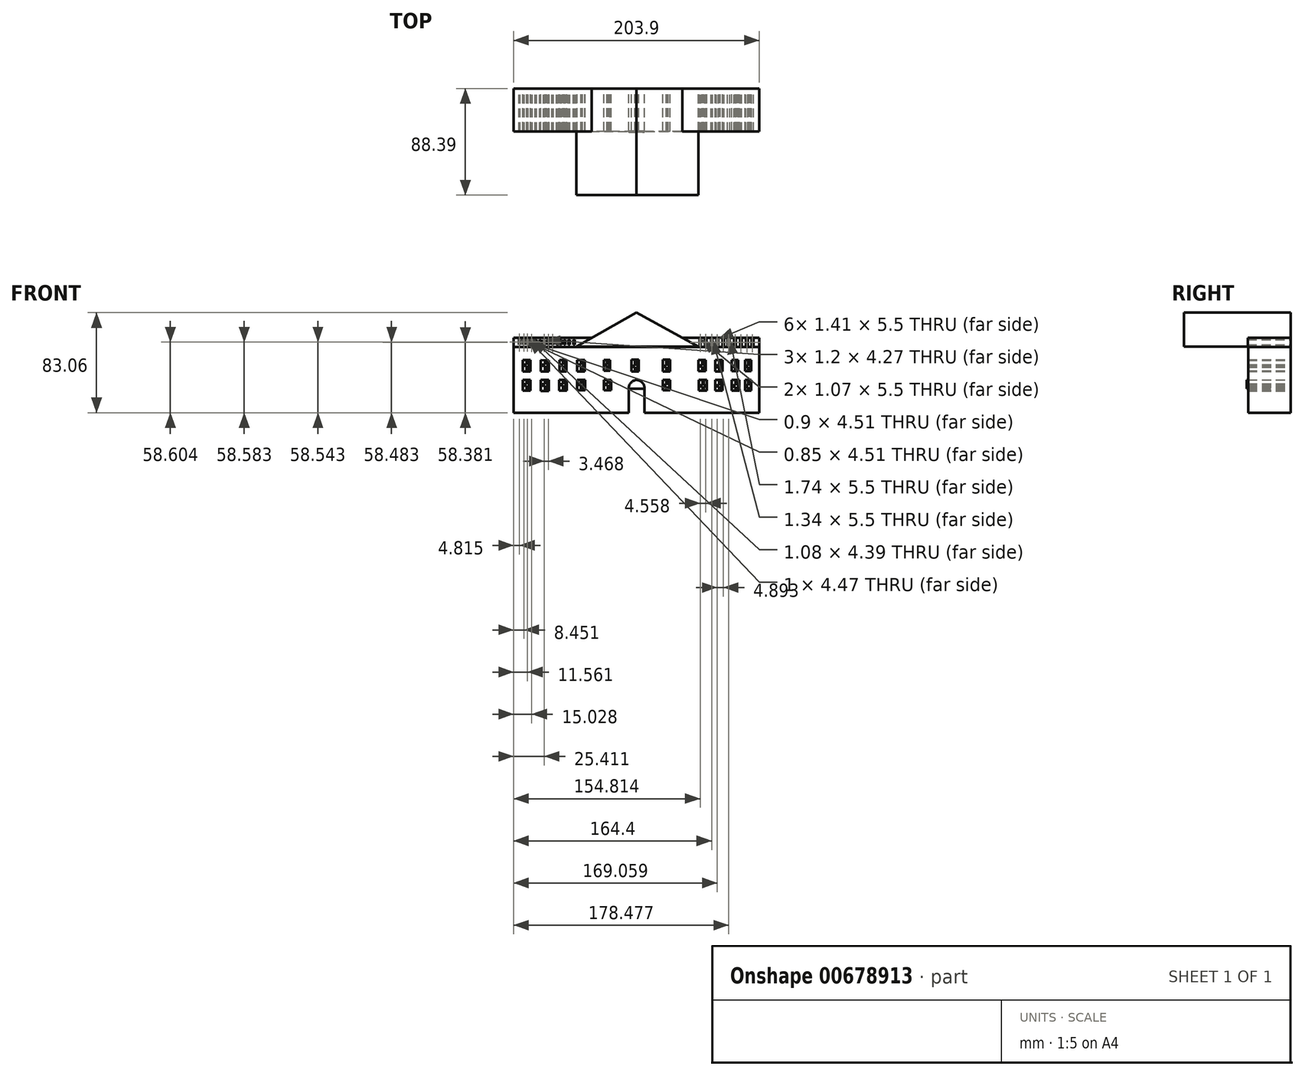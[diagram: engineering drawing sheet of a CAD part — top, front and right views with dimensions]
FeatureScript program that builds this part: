
annotation { "Feature Type Name" : "Feature", "Feature Type Description" : "" }
export const myFeature = defineFeature(function(context is Context, id is Id, definition is map)
    precondition{}
    {
        {
            var Q0;
            Q0=qCreatedBy(makeId("Front.planeOp"),FACE);
            var sketch = newSketch(context, id + "F0", { "sketchPlane" : qUnion([Q0])});
            skLineSegment(sketch, "E0.bottom", {"start": v(-101.95, -27.21) * mm, "end": v(101.95, -27.21) * mm});
            skLineSegment(sketch, "E0.top", {"start": v(-101.95, 27.21) * mm, "end": v(101.95, 27.21) * mm});
            skLineSegment(sketch, "E0.left", {"start": v(-101.95, -27.21) * mm, "end": v(-101.95, 27.21) * mm});
            skLineSegment(sketch, "E0.right", {"start": v(101.95, -27.21) * mm, "end": v(101.95, 27.21) * mm});
            skPoint(sketch, "E0.middle", {"position": v(0, 0) * mm});
            skLineSegment(sketch, "E1", {"start": v(-63.99, 16.59) * mm, "end": v(-63.99, 7.1) * mm});
            skLineSegment(sketch, "E2", {"start": v(-63.99, 16.59) * mm, "end": v(-58.11, 16.59) * mm});
            skLineSegment(sketch, "E3", {"start": v(-58.11, 16.59) * mm, "end": v(-58.11, 7.1) * mm});
            skLineSegment(sketch, "E4", {"start": v(-63.99, 7.1) * mm, "end": v(-58.11, 7.1) * mm});
            skLineSegment(sketch, "E5", {"start": v(-64.18, 0) * mm, "end": v(-64.18, -9) * mm});
            skLineSegment(sketch, "E6", {"start": v(-64.18, 0) * mm, "end": v(-57.73, 0) * mm});
            skLineSegment(sketch, "E7", {"start": v(-57.73, 0) * mm, "end": v(-57.73, -9) * mm});
            skLineSegment(sketch, "E8", {"start": v(-64.18, -9) * mm, "end": v(-57.73, -9) * mm});
            skLineSegment(sketch, "E9", {"start": v(51.48, 16.59) * mm, "end": v(51.48, 7.3) * mm});
            skLineSegment(sketch, "E10", {"start": v(51.48, 16.59) * mm, "end": v(57.54, 16.59) * mm});
            skLineSegment(sketch, "E11", {"start": v(57.54, 16.59) * mm, "end": v(57.54, 7.3) * mm});
            skLineSegment(sketch, "E12", {"start": v(57.54, 7.3) * mm, "end": v(51.48, 7.3) * mm});
            skLineSegment(sketch, "E13", {"start": v(51.67, 0) * mm, "end": v(51.67, -8.82) * mm});
            skLineSegment(sketch, "E14", {"start": v(51.67, -8.82) * mm, "end": v(58.3, -8.82) * mm});
            skLineSegment(sketch, "E15", {"start": v(58.3, -8.82) * mm, "end": v(58.3, 0) * mm});
            skLineSegment(sketch, "E16", {"start": v(58.3, 0) * mm, "end": v(51.67, 0) * mm});
            skLineSegment(sketch, "E17", {"start": v(-63.99, 11.85) * mm, "end": v(-58.11, 11.85) * mm});
            skLineSegment(sketch, "E18", {"start": v(-64.18, -4.5) * mm, "end": v(-57.73, -4.5) * mm});
            skLineSegment(sketch, "E19", {"start": v(51.48, 11.94) * mm, "end": v(57.54, 11.94) * mm});
            skLineSegment(sketch, "E20", {"start": v(54.98, 0) * mm, "end": v(54.98, -8.82) * mm});
            skLineSegment(sketch, "E21", {"start": v(51.67, -4.4) * mm, "end": v(58.3, -4.4) * mm});
            skLineSegment(sketch, "E22", {"start": v(-49.4, 16.59) * mm, "end": v(-49.4, 6.93) * mm});
            skLineSegment(sketch, "E23", {"start": v(-49.4, 16.59) * mm, "end": v(-42.94, 16.59) * mm});
            skLineSegment(sketch, "E24", {"start": v(-42.94, 16.59) * mm, "end": v(-42.94, 6.92) * mm});
            skLineSegment(sketch, "E25", {"start": v(-49.4, 6.93) * mm, "end": v(-42.94, 6.92) * mm});
            skLineSegment(sketch, "E26", {"start": v(-49.4, 11.76) * mm, "end": v(-42.94, 11.75) * mm});
            skLineSegment(sketch, "E27", {"start": v(-49.4, 0) * mm, "end": v(-49.4, -8.46) * mm});
            skLineSegment(sketch, "E28", {"start": v(-49.4, 0) * mm, "end": v(-42.56, 0) * mm});
            skLineSegment(sketch, "E29", {"start": v(-42.56, 0) * mm, "end": v(-42.56, -8.46) * mm});
            skLineSegment(sketch, "E30", {"start": v(-42.56, -8.46) * mm, "end": v(-49.4, -8.46) * mm});
            skLineSegment(sketch, "E31", {"start": v(-49.4, -4.23) * mm, "end": v(-42.56, -4.23) * mm});
            skLineSegment(sketch, "E32", {"start": v(-72.65, 16.38) * mm, "end": v(-72.65, 6.92) * mm});
            skLineSegment(sketch, "E33", {"start": v(-72.65, 6.92) * mm, "end": v(-79.35, 6.92) * mm});
            skLineSegment(sketch, "E34", {"start": v(-79.35, 6.92) * mm, "end": v(-79.35, 16.38) * mm});
            skLineSegment(sketch, "E35", {"start": v(-79.35, 16.38) * mm, "end": v(-72.65, 16.38) * mm});
            skLineSegment(sketch, "E36", {"start": v(-87.88, 6.92) * mm, "end": v(-87.88, 16.59) * mm});
            skLineSegment(sketch, "E37", {"start": v(-87.88, 16.59) * mm, "end": v(-94.32, 16.59) * mm});
            skLineSegment(sketch, "E38", {"start": v(-94.32, 16.59) * mm, "end": v(-94.32, 6.92) * mm});
            skLineSegment(sketch, "E39", {"start": v(-94.32, 6.92) * mm, "end": v(-87.88, 6.92) * mm});
            skLineSegment(sketch, "E40", {"start": v(-72.65, 0) * mm, "end": v(-72.71, -9.2) * mm});
            skLineSegment(sketch, "E41", {"start": v(-72.71, -9.2) * mm, "end": v(-79.35, -9.2) * mm});
            skLineSegment(sketch, "E42", {"start": v(-79.35, -9.2) * mm, "end": v(-79.35, 0) * mm});
            skLineSegment(sketch, "E43", {"start": v(-79.35, 0) * mm, "end": v(-72.65, 0) * mm});
            skLineSegment(sketch, "E44", {"start": v(-94.32, 0) * mm, "end": v(-94.32, -9) * mm});
            skLineSegment(sketch, "E45", {"start": v(-94.32, -9) * mm, "end": v(-87.88, -9) * mm});
            skLineSegment(sketch, "E46", {"start": v(-87.88, -9) * mm, "end": v(-87.88, 0) * mm});
            skLineSegment(sketch, "E47", {"start": v(-87.88, 0) * mm, "end": v(-94.32, 0) * mm});
            skLineSegment(sketch, "E48", {"start": v(65.32, 16.59) * mm, "end": v(65.32, 7.1) * mm});
            skLineSegment(sketch, "E49", {"start": v(65.32, 7.1) * mm, "end": v(71.46, 7.1) * mm});
            skLineSegment(sketch, "E50", {"start": v(71.46, 7.1) * mm, "end": v(71.46, 16.59) * mm});
            skLineSegment(sketch, "E51", {"start": v(65.32, 16.59) * mm, "end": v(71.46, 16.59) * mm});
            skLineSegment(sketch, "E52", {"start": v(65.32, 0) * mm, "end": v(71.46, 0) * mm});
            skLineSegment(sketch, "E53", {"start": v(71.46, 0) * mm, "end": v(71.46, -8.83) * mm});
            skLineSegment(sketch, "E54", {"start": v(71.46, -8.83) * mm, "end": v(65.32, -8.83) * mm});
            skLineSegment(sketch, "E55", {"start": v(65.32, 0) * mm, "end": v(65.32, -8.83) * mm});
            skLineSegment(sketch, "E56", {"start": v(78.97, 16.59) * mm, "end": v(78.97, 7.22) * mm});
            skLineSegment(sketch, "E57", {"start": v(78.97, 7.22) * mm, "end": v(84.47, 7.22) * mm});
            skLineSegment(sketch, "E58", {"start": v(84.47, 7.22) * mm, "end": v(84.47, 16.59) * mm});
            skLineSegment(sketch, "E59", {"start": v(84.47, 16.59) * mm, "end": v(78.97, 16.59) * mm});
            skLineSegment(sketch, "E60", {"start": v(78.97, 0) * mm, "end": v(78.97, -9) * mm});
            skLineSegment(sketch, "E61", {"start": v(78.97, -9) * mm, "end": v(85.22, -9) * mm});
            skLineSegment(sketch, "E62", {"start": v(85.22, -9) * mm, "end": v(85.22, 0) * mm});
            skLineSegment(sketch, "E63", {"start": v(85.22, 0) * mm, "end": v(78.97, 0) * mm});
            skLineSegment(sketch, "E64", {"start": v(-91.1, 16.59) * mm, "end": v(-91.1, 6.92) * mm});
            skLineSegment(sketch, "E65", {"start": v(-94.32, 11.76) * mm, "end": v(-87.88, 11.76) * mm});
            skLineSegment(sketch, "E66", {"start": v(-76, 16.38) * mm, "end": v(-76, 6.92) * mm});
            skPoint(sketch, "E67.endSnap0", {"position": v(-72.65, 11.65) * mm});
            skLineSegment(sketch, "E68", {"start": v(-61.05, 16.59) * mm, "end": v(-61.05, 7.1) * mm});
            skLineSegment(sketch, "E69", {"start": v(-46.17, 16.59) * mm, "end": v(-46.17, 6.93) * mm});
            skLineSegment(sketch, "E70", {"start": v(-91.1, 0) * mm, "end": v(-91.1, -9) * mm});
            skLineSegment(sketch, "E71", {"start": v(-94.32, -4.6) * mm, "end": v(-87.88, -4.6) * mm});
            skLineSegment(sketch, "E72", {"start": v(-76, 0) * mm, "end": v(-76.03, -9.2) * mm});
            skLineSegment(sketch, "E73", {"start": v(-79.35, -4.6) * mm, "end": v(-72.68, -4.6) * mm});
            skLineSegment(sketch, "E74", {"start": v(90.03, 16.59) * mm, "end": v(90.03, 7.45) * mm});
            skLineSegment(sketch, "E75", {"start": v(90.03, 7.45) * mm, "end": v(95.26, 7.45) * mm});
            skLineSegment(sketch, "E76", {"start": v(95.26, 7.45) * mm, "end": v(95.26, 16.59) * mm});
            skLineSegment(sketch, "E77", {"start": v(95.26, 16.59) * mm, "end": v(90.03, 16.59) * mm});
            skLineSegment(sketch, "E78", {"start": v(90.03, 0) * mm, "end": v(90.03, -9) * mm});
            skLineSegment(sketch, "E79", {"start": v(90.03, -9) * mm, "end": v(95.26, -9) * mm});
            skLineSegment(sketch, "E80", {"start": v(95.26, -9) * mm, "end": v(95.26, 0) * mm});
            skLineSegment(sketch, "E81", {"start": v(95.26, 0) * mm, "end": v(90.03, 0) * mm});
            skLineSegment(sketch, "E82", {"start": v(54.5, 16.59) * mm, "end": v(54.5, 7.3) * mm});
            skLineSegment(sketch, "E83", {"start": v(65.32, 11.94) * mm, "end": v(71.46, 11.94) * mm});
            skLineSegment(sketch, "E84", {"start": v(68.39, 16.59) * mm, "end": v(68.39, 7.1) * mm});
            skLineSegment(sketch, "E85", {"start": v(78.97, 11.9) * mm, "end": v(84.47, 11.9) * mm});
            skLineSegment(sketch, "E86", {"start": v(81.72, 16.59) * mm, "end": v(81.72, 7.22) * mm});
            skLineSegment(sketch, "E87", {"start": v(92.64, 16.59) * mm, "end": v(92.64, 7.45) * mm});
            skLineSegment(sketch, "E88", {"start": v(90.03, 11.9) * mm, "end": v(95.26, 11.9) * mm});
            skLineSegment(sketch, "E89", {"start": v(68.39, 0) * mm, "end": v(68.39, -8.83) * mm});
            skLineSegment(sketch, "E90", {"start": v(65.32, -4.42) * mm, "end": v(71.46, -4.42) * mm});
            skLineSegment(sketch, "E91", {"start": v(82.1, 0) * mm, "end": v(82.1, -9) * mm});
            skLineSegment(sketch, "E92", {"start": v(78.97, -4.5) * mm, "end": v(85.22, -4.5) * mm});
            skLineSegment(sketch, "E93", {"start": v(92.64, 0) * mm, "end": v(92.64, -9) * mm});
            skLineSegment(sketch, "E94", {"start": v(90.03, -4.5) * mm, "end": v(95.26, -4.5) * mm});
            skLineSegment(sketch, "E95", {"start": v(-60.96, 0) * mm, "end": v(-60.96, -9) * mm});
            skLineSegment(sketch, "E96", {"start": v(-45.98, 0) * mm, "end": v(-45.98, -8.46) * mm});
            skLineSegment(sketch, "E97.bottom", {"start": v(-27.02, 7.5) * mm, "end": v(-21.9, 7.5) * mm});
            skLineSegment(sketch, "E97.top", {"start": v(-27.02, 16.4) * mm, "end": v(-21.9, 16.4) * mm});
            skLineSegment(sketch, "E97.left", {"start": v(-27.02, 7.5) * mm, "end": v(-27.02, 16.4) * mm});
            skLineSegment(sketch, "E97.right", {"start": v(-21.9, 7.5) * mm, "end": v(-21.9, 16.4) * mm});
            skLineSegment(sketch, "E98.bottom", {"start": v(-4.27, 16.78) * mm, "end": v(1.8, 16.78) * mm});
            skLineSegment(sketch, "E98.top", {"start": v(-4.27, 6.93) * mm, "end": v(1.8, 6.93) * mm});
            skLineSegment(sketch, "E98.left", {"start": v(-4.27, 16.78) * mm, "end": v(-4.27, 6.93) * mm});
            skLineSegment(sketch, "E98.right", {"start": v(1.8, 16.78) * mm, "end": v(1.8, 6.93) * mm});
            skLineSegment(sketch, "E99.bottom", {"start": v(21.7, 16.78) * mm, "end": v(27.78, 16.78) * mm});
            skLineSegment(sketch, "E99.top", {"start": v(21.7, 6.93) * mm, "end": v(27.78, 6.93) * mm});
            skLineSegment(sketch, "E99.left", {"start": v(21.7, 16.78) * mm, "end": v(21.7, 6.93) * mm});
            skLineSegment(sketch, "E99.right", {"start": v(27.78, 16.78) * mm, "end": v(27.78, 6.93) * mm});
            skLineSegment(sketch, "E100.bottom", {"start": v(-27.02, -8.46) * mm, "end": v(-20.95, -8.46) * mm});
            skLineSegment(sketch, "E100.top", {"start": v(-27.02, 0) * mm, "end": v(-20.95, 0) * mm});
            skLineSegment(sketch, "E100.left", {"start": v(-27.02, -8.46) * mm, "end": v(-27.02, 0) * mm});
            skLineSegment(sketch, "E100.right", {"start": v(-20.95, -8.46) * mm, "end": v(-20.95, 0) * mm});
            skLineSegment(sketch, "E101.bottom", {"start": v(21.7, 0) * mm, "end": v(27.78, 0) * mm});
            skLineSegment(sketch, "E101.top", {"start": v(21.7, -8.46) * mm, "end": v(27.78, -8.46) * mm});
            skLineSegment(sketch, "E101.left", {"start": v(21.7, 0) * mm, "end": v(21.7, -8.46) * mm});
            skLineSegment(sketch, "E101.right", {"start": v(27.78, 0) * mm, "end": v(27.78, -8.46) * mm});
            skLineSegment(sketch, "E102.bottom", {"start": v(-6.49, -7.17) * mm, "end": v(6.77, -7.17) * mm});
            skLineSegment(sketch, "E102.top", {"start": v(-6.49, -27.21) * mm, "end": v(6.77, -27.21) * mm});
            skLineSegment(sketch, "E102.left", {"start": v(-6.49, -7.17) * mm, "end": v(-6.49, -27.21) * mm});
            skLineSegment(sketch, "E102.right", {"start": v(6.77, -7.17) * mm, "end": v(6.77, -27.21) * mm});
            skArc(sketch, "E103", {"start": v(-6.49, -7.17) * mm, "mid": v(-4.62, -2.34) * mm, "end": v(0, 0) * mm});
            skArc(sketch, "E104", {"start": v(6.77, -7.17) * mm, "mid": v(4.8, -2.24) * mm, "end": v(0, 0) * mm});
            skLineSegment(sketch, "E105", {"start": v(-4.27, 11.85) * mm, "end": v(1.8, 11.85) * mm});
            skLineSegment(sketch, "E106", {"start": v(-1.23, 16.78) * mm, "end": v(-1.23, 6.93) * mm});
            skLineSegment(sketch, "E107", {"start": v(-24.46, 16.4) * mm, "end": v(-24.46, 7.5) * mm});
            skLineSegment(sketch, "E108", {"start": v(-27.02, 11.95) * mm, "end": v(-21.9, 11.95) * mm});
            skLineSegment(sketch, "E109", {"start": v(-23.98, 0) * mm, "end": v(-23.98, -8.46) * mm});
            skLineSegment(sketch, "E110", {"start": v(-27.02, -4.23) * mm, "end": v(-20.95, -4.23) * mm});
            skLineSegment(sketch, "E111", {"start": v(24.74, 16.78) * mm, "end": v(24.74, 6.93) * mm});
            skLineSegment(sketch, "E112", {"start": v(21.7, 11.85) * mm, "end": v(27.78, 11.85) * mm});
            skLineSegment(sketch, "E113", {"start": v(24.74, 0) * mm, "end": v(24.74, -8.46) * mm});
            skLineSegment(sketch, "E114", {"start": v(21.7, -4.23) * mm, "end": v(27.78, -4.23) * mm});
            skLineSegment(sketch, "E115", {"start": v(-35.12, 27.05) * mm, "end": v(-35.12, -26.82) * mm});
            skLineSegment(sketch, "E116", {"start": v(-37.36, 27.05) * mm, "end": v(-37.36, -26.82) * mm});
            skLineSegment(sketch, "E117", {"start": v(-32.96, -26.82) * mm, "end": v(-32.96, 27.05) * mm});
            skLineSegment(sketch, "E118", {"start": v(-15.86, -26.53) * mm, "end": v(-15.86, 26.88) * mm});
            skLineSegment(sketch, "E119", {"start": v(-10.16, 26.88) * mm, "end": v(-10.16, -26.53) * mm});
            skLineSegment(sketch, "E120", {"start": v(12.5, 26.79) * mm, "end": v(12.5, -26.62) * mm});
            skLineSegment(sketch, "E121", {"start": v(16.1, 26.98) * mm, "end": v(16.1, -26.43) * mm});
            skLineSegment(sketch, "E122", {"start": v(9.23, 26.83) * mm, "end": v(9.23, -26.58) * mm});
            skLineSegment(sketch, "E123", {"start": v(40, 27.01) * mm, "end": v(40, -26.4) * mm});
            skLineSegment(sketch, "E124", {"start": v(33.56, 26.92) * mm, "end": v(33.56, -26.49) * mm});
            skLineSegment(sketch, "E125", {"start": v(-94.32, 12.63) * mm, "end": v(-87.88, 12.63) * mm});
            skLineSegment(sketch, "E126", {"start": v(-72.65, 11.65) * mm, "end": v(-79.35, 11.65) * mm});
            skLineSegment(sketch, "E127", {"start": v(-79.35, 12.63) * mm, "end": v(-72.65, 12.63) * mm});
            skLineSegment(sketch, "E128", {"start": v(-63.99, 12.63) * mm, "end": v(-58.11, 12.63) * mm});
            skLineSegment(sketch, "E129", {"start": v(-49.4, 12.63) * mm, "end": v(-42.94, 12.63) * mm});
            skLineSegment(sketch, "E130", {"start": v(-27.02, 12.63) * mm, "end": v(-21.9, 12.63) * mm});
            skLineSegment(sketch, "E131", {"start": v(-94.32, -3.52) * mm, "end": v(-87.88, -3.52) * mm});
            skLineSegment(sketch, "E132", {"start": v(-79.35, -3.52) * mm, "end": v(-72.67, -3.52) * mm});
            skLineSegment(sketch, "E133", {"start": v(-64.18, -3.52) * mm, "end": v(-57.73, -3.52) * mm});
            skLineSegment(sketch, "E134", {"start": v(-49.4, -3.15) * mm, "end": v(-42.56, -3.15) * mm});
            skLineSegment(sketch, "E135", {"start": v(-27.02, -3.15) * mm, "end": v(-20.95, -3.15) * mm});
            skLineSegment(sketch, "E136", {"start": v(-90.24, 16.59) * mm, "end": v(-90.24, 6.92) * mm});
            skLineSegment(sketch, "E137", {"start": v(-74.78, 16.38) * mm, "end": v(-74.79, 6.92) * mm});
            skLineSegment(sketch, "E138", {"start": v(-90.06, 0) * mm, "end": v(-90.06, -9) * mm});
            skLineSegment(sketch, "E139", {"start": v(-59.94, 16.59) * mm, "end": v(-59.94, 7.1) * mm});
            skLineSegment(sketch, "E140", {"start": v(-74.93, 0) * mm, "end": v(-74.93, -9.2) * mm});
            skLineSegment(sketch, "E141", {"start": v(-59.8, 0) * mm, "end": v(-59.8, -9) * mm});
            skLineSegment(sketch, "E142", {"start": v(-45.1, 16.59) * mm, "end": v(-45.12, 6.92) * mm});
            skLineSegment(sketch, "E143", {"start": v(-44.74, 0) * mm, "end": v(-44.74, -8.46) * mm});
            skLineSegment(sketch, "E144", {"start": v(-23.61, 16.4) * mm, "end": v(-23.61, 7.5) * mm});
            skLineSegment(sketch, "E145", {"start": v(-22.73, 0) * mm, "end": v(-22.73, -8.46) * mm});
            skLineSegment(sketch, "E146", {"start": v(-4.27, 10.73) * mm, "end": v(1.8, 10.73) * mm});
            skLineSegment(sketch, "E147", {"start": v(0, 16.78) * mm, "end": v(0, 6.93) * mm});
            skLineSegment(sketch, "E148", {"start": v(26.02, 16.78) * mm, "end": v(26.02, 6.93) * mm});
            skLineSegment(sketch, "E149", {"start": v(21.7, 10.73) * mm, "end": v(27.78, 10.73) * mm});
            skLineSegment(sketch, "E150", {"start": v(26.24, 0) * mm, "end": v(26.24, -8.46) * mm});
            skLineSegment(sketch, "E151", {"start": v(21.7, -5.43) * mm, "end": v(27.78, -5.43) * mm});
            skLineSegment(sketch, "E152", {"start": v(55.41, 16.59) * mm, "end": v(55.41, 7.3) * mm});
            skLineSegment(sketch, "E153", {"start": v(51.48, 11.02) * mm, "end": v(57.54, 11.02) * mm});
            skLineSegment(sketch, "E154", {"start": v(56, 0) * mm, "end": v(56, -8.82) * mm});
            skLineSegment(sketch, "E155", {"start": v(51.67, -5.43) * mm, "end": v(58.3, -5.43) * mm});
            skLineSegment(sketch, "E156", {"start": v(69.45, 0) * mm, "end": v(69.45, -8.83) * mm});
            skLineSegment(sketch, "E157", {"start": v(65.32, -5.5) * mm, "end": v(71.46, -5.5) * mm});
            skLineSegment(sketch, "E158", {"start": v(69.52, 16.59) * mm, "end": v(69.52, 7.1) * mm});
            skLineSegment(sketch, "E159", {"start": v(65.32, 10.65) * mm, "end": v(71.46, 10.65) * mm});
            skLineSegment(sketch, "E160", {"start": v(82.75, 16.59) * mm, "end": v(82.75, 7.22) * mm});
            skLineSegment(sketch, "E161", {"start": v(78.97, 10.8) * mm, "end": v(84.47, 10.8) * mm});
            skLineSegment(sketch, "E162", {"start": v(83.4, 0) * mm, "end": v(83.4, -9) * mm});
            skLineSegment(sketch, "E163", {"start": v(78.97, -5.72) * mm, "end": v(85.22, -5.72) * mm});
            skLineSegment(sketch, "E164", {"start": v(93.93, 0) * mm, "end": v(93.93, -9) * mm});
            skLineSegment(sketch, "E165", {"start": v(90.03, -5.94) * mm, "end": v(95.26, -5.94) * mm});
            skLineSegment(sketch, "E166", {"start": v(93.5, 16.59) * mm, "end": v(93.6, 7.45) * mm});
            skLineSegment(sketch, "E167", {"start": v(90.03, 10.8) * mm, "end": v(95.26, 10.8) * mm});
            skLineSegment(sketch, "E168", {"start": v(36.76, -26.49) * mm, "end": v(36.76, 26.92) * mm});
            skLineSegment(sketch, "E169", {"start": v(0, 55.85) * mm, "end": v(-49.85, 27.58) * mm});
            skLineSegment(sketch, "E170", {"start": v(0, 55.85) * mm, "end": v(51.4, 27.5) * mm});
            skLineSegment(sketch, "E171", {"start": v(-49.85, 27.58) * mm, "end": v(51.4, 27.5) * mm});
            skLineSegment(sketch, "E172", {"start": v(-13.08, 26.64) * mm, "end": v(-13.08, -26.53) * mm});
            skLineSegment(sketch, "E173", {"start": v(-101.95, 27.21) * mm, "end": v(-101.95, 34.84) * mm});
            skLineSegment(sketch, "E174", {"start": v(-101.95, 34.84) * mm, "end": v(-37.05, 34.84) * mm});
            skLineSegment(sketch, "E175", {"start": v(101.95, 27.21) * mm, "end": v(101.95, 34.84) * mm});
            skLineSegment(sketch, "E176", {"start": v(38.1, 34.84) * mm, "end": v(101.95, 34.84) * mm});
            skLineSegment(sketch, "E177", {"start": v(-97.59, 33.65) * mm, "end": v(-97.59, 29.14) * mm});
            skLineSegment(sketch, "E178", {"start": v(-97.59, 29.14) * mm, "end": v(-96.68, 29.14) * mm});
            skLineSegment(sketch, "E179", {"start": v(-96.68, 29.14) * mm, "end": v(-96.68, 33.65) * mm});
            skLineSegment(sketch, "E180", {"start": v(-96.68, 33.65) * mm, "end": v(-97.59, 33.65) * mm});
            skLineSegment(sketch, "E181", {"start": v(-93.92, 33.65) * mm, "end": v(-93.92, 29.14) * mm});
            skLineSegment(sketch, "E182", {"start": v(-93.92, 33.65) * mm, "end": v(-93.08, 33.65) * mm});
            skLineSegment(sketch, "E183", {"start": v(-93.08, 33.65) * mm, "end": v(-93.08, 29.14) * mm});
            skLineSegment(sketch, "E184", {"start": v(-93.92, 29.14) * mm, "end": v(-93.08, 29.14) * mm});
            skLineSegment(sketch, "E185.bottom", {"start": v(-90.89, 29.14) * mm, "end": v(-89.9, 29.14) * mm});
            skLineSegment(sketch, "E185.top", {"start": v(-90.89, 33.6) * mm, "end": v(-89.9, 33.6) * mm});
            skLineSegment(sketch, "E185.left", {"start": v(-90.89, 29.14) * mm, "end": v(-90.89, 33.6) * mm});
            skLineSegment(sketch, "E185.right", {"start": v(-89.9, 29.14) * mm, "end": v(-89.9, 33.6) * mm});
            skLineSegment(sketch, "E186.bottom", {"start": v(-87.46, 29.14) * mm, "end": v(-86.38, 29.14) * mm});
            skLineSegment(sketch, "E186.top", {"start": v(-87.46, 33.53) * mm, "end": v(-86.38, 33.53) * mm});
            skLineSegment(sketch, "E186.left", {"start": v(-87.46, 29.14) * mm, "end": v(-87.46, 33.53) * mm});
            skLineSegment(sketch, "E186.right", {"start": v(-86.38, 29.14) * mm, "end": v(-86.38, 33.53) * mm});
            skLineSegment(sketch, "E187.bottom", {"start": v(-84.03, 29.14) * mm, "end": v(-82.8, 29.14) * mm});
            skLineSegment(sketch, "E187.top", {"start": v(-84.03, 33.45) * mm, "end": v(-82.8, 33.45) * mm});
            skLineSegment(sketch, "E187.left", {"start": v(-84.03, 29.14) * mm, "end": v(-84.03, 33.45) * mm});
            skLineSegment(sketch, "E187.right", {"start": v(-82.8, 29.14) * mm, "end": v(-82.8, 33.45) * mm});
            skLineSegment(sketch, "E188.bottom", {"start": v(-80.29, 29.14) * mm, "end": v(-79.33, 29.14) * mm});
            skLineSegment(sketch, "E188.top", {"start": v(-80.29, 33.4) * mm, "end": v(-79.33, 33.4) * mm});
            skLineSegment(sketch, "E188.left", {"start": v(-80.29, 29.14) * mm, "end": v(-80.29, 33.4) * mm});
            skLineSegment(sketch, "E188.right", {"start": v(-79.33, 29.14) * mm, "end": v(-79.33, 33.4) * mm});
            skLineSegment(sketch, "E189.bottom", {"start": v(-77.14, 29.14) * mm, "end": v(-75.94, 29.14) * mm});
            skLineSegment(sketch, "E189.top", {"start": v(-77.14, 33.4) * mm, "end": v(-75.94, 33.4) * mm});
            skLineSegment(sketch, "E189.left", {"start": v(-77.14, 29.14) * mm, "end": v(-77.14, 33.4) * mm});
            skLineSegment(sketch, "E189.right", {"start": v(-75.94, 29.14) * mm, "end": v(-75.94, 33.4) * mm});
            skLineSegment(sketch, "E190.bottom", {"start": v(-73.67, 29.14) * mm, "end": v(-72.47, 29.14) * mm});
            skLineSegment(sketch, "E190.top", {"start": v(-73.67, 33.4) * mm, "end": v(-72.47, 33.4) * mm});
            skLineSegment(sketch, "E190.left", {"start": v(-73.67, 29.14) * mm, "end": v(-73.67, 33.4) * mm});
            skLineSegment(sketch, "E190.right", {"start": v(-72.47, 29.14) * mm, "end": v(-72.47, 33.4) * mm});
            skLineSegment(sketch, "E191.bottom", {"start": v(-70.12, 29.14) * mm, "end": v(-68.93, 29.14) * mm});
            skLineSegment(sketch, "E191.top", {"start": v(-70.12, 33.4) * mm, "end": v(-68.93, 33.4) * mm});
            skLineSegment(sketch, "E191.left", {"start": v(-70.12, 29.14) * mm, "end": v(-70.12, 33.4) * mm});
            skLineSegment(sketch, "E191.right", {"start": v(-68.93, 29.14) * mm, "end": v(-68.93, 33.4) * mm});
            skLineSegment(sketch, "E192.bottom", {"start": v(-66.29, 29.14) * mm, "end": v(-65.25, 29.14) * mm});
            skLineSegment(sketch, "E192.top", {"start": v(-66.29, 33.4) * mm, "end": v(-65.25, 33.4) * mm});
            skLineSegment(sketch, "E192.left", {"start": v(-66.29, 29.14) * mm, "end": v(-66.29, 33.4) * mm});
            skLineSegment(sketch, "E192.right", {"start": v(-65.25, 29.14) * mm, "end": v(-65.25, 33.4) * mm});
            skLineSegment(sketch, "E193.bottom", {"start": v(-63.17, 29.14) * mm, "end": v(-62.2, 29.14) * mm});
            skLineSegment(sketch, "E193.top", {"start": v(-63.17, 33.4) * mm, "end": v(-62.2, 33.4) * mm});
            skLineSegment(sketch, "E193.left", {"start": v(-63.17, 29.14) * mm, "end": v(-63.17, 33.4) * mm});
            skLineSegment(sketch, "E193.right", {"start": v(-62.2, 29.14) * mm, "end": v(-62.2, 33.4) * mm});
            skLineSegment(sketch, "E194.bottom", {"start": v(-60.14, 29.14) * mm, "end": v(-58.97, 29.14) * mm});
            skLineSegment(sketch, "E194.top", {"start": v(-60.14, 33.4) * mm, "end": v(-58.97, 33.4) * mm});
            skLineSegment(sketch, "E194.left", {"start": v(-60.14, 29.14) * mm, "end": v(-60.14, 33.4) * mm});
            skLineSegment(sketch, "E194.right", {"start": v(-58.97, 29.14) * mm, "end": v(-58.97, 33.4) * mm});
            skLineSegment(sketch, "E195.bottom", {"start": v(-56.6, 29.14) * mm, "end": v(-55.37, 29.14) * mm});
            skLineSegment(sketch, "E195.top", {"start": v(-56.6, 33.4) * mm, "end": v(-55.37, 33.4) * mm});
            skLineSegment(sketch, "E195.left", {"start": v(-56.6, 29.14) * mm, "end": v(-56.6, 33.4) * mm});
            skLineSegment(sketch, "E195.right", {"start": v(-55.37, 29.14) * mm, "end": v(-55.37, 33.4) * mm});
            skLineSegment(sketch, "E196.bottom", {"start": v(-52.31, 29.1) * mm, "end": v(-51.3, 29.1) * mm});
            skLineSegment(sketch, "E196.top", {"start": v(-52.31, 33.45) * mm, "end": v(-51.3, 33.45) * mm});
            skLineSegment(sketch, "E196.left", {"start": v(-52.31, 29.1) * mm, "end": v(-52.31, 33.45) * mm});
            skLineSegment(sketch, "E196.right", {"start": v(-51.3, 29.1) * mm, "end": v(-51.3, 33.45) * mm});
            skLineSegment(sketch, "E197.bottom", {"start": v(52.33, 28.42) * mm, "end": v(53.4, 28.42) * mm});
            skLineSegment(sketch, "E197.top", {"start": v(52.33, 33.92) * mm, "end": v(53.4, 33.92) * mm});
            skLineSegment(sketch, "E197.left", {"start": v(52.33, 28.42) * mm, "end": v(52.33, 33.92) * mm});
            skLineSegment(sketch, "E197.right", {"start": v(53.4, 28.42) * mm, "end": v(53.4, 33.92) * mm});
            skLineSegment(sketch, "E198.bottom", {"start": v(56.89, 28.42) * mm, "end": v(57.96, 28.42) * mm});
            skLineSegment(sketch, "E198.top", {"start": v(56.89, 33.92) * mm, "end": v(57.96, 33.92) * mm});
            skLineSegment(sketch, "E198.left", {"start": v(56.89, 28.42) * mm, "end": v(56.89, 33.92) * mm});
            skLineSegment(sketch, "E198.right", {"start": v(57.96, 28.42) * mm, "end": v(57.96, 33.92) * mm});
            skLineSegment(sketch, "E199.bottom", {"start": v(61.78, 28.42) * mm, "end": v(63.12, 28.42) * mm});
            skLineSegment(sketch, "E199.top", {"start": v(61.78, 33.92) * mm, "end": v(63.12, 33.92) * mm});
            skLineSegment(sketch, "E199.left", {"start": v(61.78, 28.42) * mm, "end": v(61.78, 33.92) * mm});
            skLineSegment(sketch, "E199.right", {"start": v(63.12, 28.42) * mm, "end": v(63.12, 33.92) * mm});
            skLineSegment(sketch, "E200.bottom", {"start": v(66.4, 28.42) * mm, "end": v(67.81, 28.42) * mm});
            skLineSegment(sketch, "E200.top", {"start": v(66.4, 33.92) * mm, "end": v(67.81, 33.92) * mm});
            skLineSegment(sketch, "E200.left", {"start": v(66.4, 28.42) * mm, "end": v(66.4, 33.92) * mm});
            skLineSegment(sketch, "E200.right", {"start": v(67.81, 28.42) * mm, "end": v(67.81, 33.92) * mm});
            skLineSegment(sketch, "E201.bottom", {"start": v(71.3, 28.42) * mm, "end": v(72.7, 28.42) * mm});
            skLineSegment(sketch, "E201.top", {"start": v(71.3, 33.92) * mm, "end": v(72.7, 33.92) * mm});
            skLineSegment(sketch, "E201.left", {"start": v(71.3, 28.42) * mm, "end": v(71.3, 33.92) * mm});
            skLineSegment(sketch, "E201.right", {"start": v(72.7, 28.42) * mm, "end": v(72.7, 33.92) * mm});
            skLineSegment(sketch, "E202.bottom", {"start": v(75.66, 28.42) * mm, "end": v(77.4, 28.42) * mm});
            skLineSegment(sketch, "E202.top", {"start": v(75.66, 33.92) * mm, "end": v(77.4, 33.92) * mm});
            skLineSegment(sketch, "E202.left", {"start": v(75.66, 28.42) * mm, "end": v(75.66, 33.92) * mm});
            skLineSegment(sketch, "E202.right", {"start": v(77.4, 28.42) * mm, "end": v(77.4, 33.92) * mm});
            skLineSegment(sketch, "E203.bottom", {"start": v(81.02, 28.42) * mm, "end": v(82.43, 28.42) * mm});
            skLineSegment(sketch, "E203.top", {"start": v(81.02, 33.92) * mm, "end": v(82.43, 33.92) * mm});
            skLineSegment(sketch, "E203.left", {"start": v(81.02, 28.42) * mm, "end": v(81.02, 33.92) * mm});
            skLineSegment(sketch, "E203.right", {"start": v(82.43, 28.42) * mm, "end": v(82.43, 33.92) * mm});
            skLineSegment(sketch, "E204.bottom", {"start": v(85.84, 28.42) * mm, "end": v(87.25, 28.42) * mm});
            skLineSegment(sketch, "E204.top", {"start": v(85.84, 33.92) * mm, "end": v(87.25, 33.92) * mm});
            skLineSegment(sketch, "E204.left", {"start": v(85.84, 28.42) * mm, "end": v(85.84, 33.92) * mm});
            skLineSegment(sketch, "E204.right", {"start": v(87.25, 28.42) * mm, "end": v(87.25, 33.92) * mm});
            skLineSegment(sketch, "E205.bottom", {"start": v(90.87, 28.42) * mm, "end": v(92.28, 28.42) * mm});
            skLineSegment(sketch, "E205.top", {"start": v(90.87, 33.92) * mm, "end": v(92.28, 33.92) * mm});
            skLineSegment(sketch, "E205.left", {"start": v(90.87, 28.42) * mm, "end": v(90.87, 33.92) * mm});
            skLineSegment(sketch, "E205.right", {"start": v(92.28, 28.42) * mm, "end": v(92.28, 33.92) * mm});
            skLineSegment(sketch, "E206.bottom", {"start": v(95.56, 28.42) * mm, "end": v(96.97, 28.42) * mm});
            skLineSegment(sketch, "E206.top", {"start": v(95.56, 33.92) * mm, "end": v(96.97, 33.92) * mm});
            skLineSegment(sketch, "E206.left", {"start": v(95.56, 28.42) * mm, "end": v(95.56, 33.92) * mm});
            skLineSegment(sketch, "E206.right", {"start": v(96.97, 28.42) * mm, "end": v(96.97, 33.92) * mm});
            skPoint(sketch, "E207.middle", {"position": v(0, -11.28) * mm});
            skLineSegment(sketch, "E208.top", {"start": v(0, -27.21) * mm, "end": v(-4.96, -27.21) * mm});
            skLineSegment(sketch, "E209.top", {"start": v(0, -27.21) * mm, "end": v(5.04, -27.21) * mm});
            skSolve(sketch);
        }
        {
            var Q0;
            Q0=sQuery(id+"F0.wireOp",EDGE,"E119");
            var Q1;
            Q1=sQuery(id+"F0.wireOp",EDGE,"E118");
            var Q2;
            Q2=sQuery(id+"F0.wireOp",EDGE,"E172");
            revolve(context, id + "F1", {"bodyType" : ToolBodyType.SURFACE, "surfaceOperationType" : NewSurfaceOperationType.NEW, "surfaceEntities" : qUnion([Q0, Q1]), "axis" : qUnion([Q2]), "revolveType" : RevolveType.FULL});
        }
        {
            var Q0;
            Q0=sQuery(id+"F0.wireOp",EDGE,"E121");
            var Q1;
            Q1=sQuery(id+"F0.wireOp",EDGE,"E122");
            var Q2;
            Q2=sQuery(id+"F0.wireOp",EDGE,"E120");
            revolve(context, id + "F2", {"bodyType" : ToolBodyType.SURFACE, "surfaceOperationType" : NewSurfaceOperationType.NEW, "surfaceEntities" : qUnion([Q0, Q1]), "axis" : qUnion([Q2]), "revolveType" : RevolveType.FULL});
        }
        {
            var Q0;
            Q0=sQuery(id+"F0.wireOp",EDGE,"E117");
            var Q1;
            Q1=sQuery(id+"F0.wireOp",EDGE,"E116");
            var Q2;
            Q2=sQuery(id+"F0.wireOp",EDGE,"E115");
            revolve(context, id + "F3", {"bodyType" : ToolBodyType.SURFACE, "surfaceOperationType" : NewSurfaceOperationType.NEW, "surfaceEntities" : qUnion([Q0, Q1]), "axis" : qUnion([Q2]), "revolveType" : RevolveType.FULL});
        }
        {
            var Q0;
            Q0=sQuery(id+"F0.wireOp",EDGE,"E123");
            var Q1;
            Q1=sQuery(id+"F0.wireOp",EDGE,"E124");
            var Q2;
            Q2=sQuery(id+"F0.wireOp",EDGE,"E168");
            revolve(context, id + "F4", {"bodyType" : ToolBodyType.SURFACE, "surfaceOperationType" : NewSurfaceOperationType.NEW, "surfaceEntities" : qUnion([Q0, Q1]), "axis" : qUnion([Q2]), "revolveType" : RevolveType.FULL});
        }
        {
            var Q0;
            Q0=makeQuery(id+"F2.opRevolve","SWEPT_BODY",BODY,{"disambiguationData":[OSD([sQuery(id+"F0.wireOp",EDGE,"E121")])]});
            var Q1;
            Q1=makeQuery(id+"F1.opRevolve","SWEPT_BODY",BODY,{"disambiguationData":[OSD([sQuery(id+"F0.wireOp",EDGE,"E119")])]});
            var Q2;
            Q2=makeQuery(id+"F4.opRevolve","SWEPT_BODY",BODY,{"disambiguationData":[OSD([sQuery(id+"F0.wireOp",EDGE,"E123")])]});
            var Q3;
            Q3=makeQuery(id+"F3.opRevolve","SWEPT_BODY",BODY,{"disambiguationData":[OSD([sQuery(id+"F0.wireOp",EDGE,"E116")])]});
            transform(context, id + "F5", {"entities" : qUnion([Q0, Q1, Q2, Q3]), "transformType" : TransformType.TRANSLATION_3D, "dx" : 0.25 * mm, "dy" : -82.3 * mm, "dz" : 0.5 * mm, "makeCopy" : true});
        }
        {
            var Q0;
            Q0=makeQuery(id+"F3.opRevolve","SWEPT_BODY",BODY,{"disambiguationData":[OSD([sQuery(id+"F0.wireOp",EDGE,"E116")])]});
            var Q1;
            Q1=makeQuery(id+"F1.opRevolve","SWEPT_BODY",BODY,{"disambiguationData":[OSD([sQuery(id+"F0.wireOp",EDGE,"E119")])]});
            var Q2;
            Q2=makeQuery(id+"F4.opRevolve","SWEPT_BODY",BODY,{"disambiguationData":[OSD([sQuery(id+"F0.wireOp",EDGE,"E123")])]});
            var Q3;
            Q3=makeQuery(id+"F2.opRevolve","SWEPT_BODY",BODY,{"disambiguationData":[OSD([sQuery(id+"F0.wireOp",EDGE,"E121")])]});
            transform(context, id + "F6", {"entities" : qUnion([Q0, Q1, Q2, Q3]), "transformType" : TransformType.TRANSLATION_3D, "dx" : 0 * mm, "dy" : -57.15 * mm, "dz" : 0.76 * mm, "makeCopy" : false});
        }
        {
            var Q0;
            Q0=makeQuery(id+"F3.opRevolve","SWEPT_BODY",BODY,{"disambiguationData":[OSD([sQuery(id+"F0.wireOp",EDGE,"E117")])]});
            var Q1;
            Q1=makeQuery(id+"F1.opRevolve","SWEPT_BODY",BODY,{"disambiguationData":[OSD([sQuery(id+"F0.wireOp",EDGE,"E118")])]});
            var Q2;
            Q2=makeQuery(id+"F2.opRevolve","SWEPT_BODY",BODY,{"disambiguationData":[OSD([sQuery(id+"F0.wireOp",EDGE,"E122")])]});
            var Q3;
            Q3=makeQuery(id+"F4.opRevolve","SWEPT_BODY",BODY,{"disambiguationData":[OSD([sQuery(id+"F0.wireOp",EDGE,"E124")])]});
            transform(context, id + "F7", {"entities" : qUnion([Q0, Q1, Q2, Q3]), "transformType" : TransformType.TRANSLATION_3D, "dx" : 0 * mm, "dy" : -44.96 * mm, "dz" : 1.27 * mm, "makeCopy" : false});
        }
        {
            var Q0;
            {var subQ250=sQuery(id+"F0.wireOp",EDGE,"E0.left");Q0=makeQuery(id+"F0.imprint","IMPRINT",FACE,{"disambiguationData":[TD([[makeQuery(id+"F0.imprint","IMPRINT",EDGE,{"derivedFrom":subQ250}),-1.0]])]});}
            extrude(context, id + "F8", {"entities" : qUnion([Q0]), "depth" : 35.3 * mm, "offsetDistance" : 25.4 * mm});
        }
        {
            var Q0;
            Q0=makeQuery(id+"F0.imprint","IMPRINT",FACE,{"disambiguationData":[TD([[makeQuery(id+"F0.imprint","IMPRINT",EDGE,{"derivedFrom":sQuery(id+"F0.wireOp",EDGE,"E169")}),1.0]])]});
            extrude(context, id + "F9", {"entities" : qUnion([Q0]), "depth" : 88.4 * mm, "offsetDistance" : 25.4 * mm});
        }
        {
            var Q0;
            {var subQ0=sQuery(id+"F0.wireOp",EDGE,"E171");Q0=makeQuery(id+"F0.imprint","IMPRINT",FACE,{"disambiguationData":[TD([[makeQuery(id+"F0.imprint","IMPRINT",EDGE,{"derivedFrom":subQ0}),-1.0]])]});}
            extrude(context, id + "F10", {"entities" : qUnion([Q0]), "depth" : 35.56 * mm, "offsetDistance" : 25.4 * mm});
        }
        {
            var Q0;
            {var subQ0=sQuery(id+"F0.wireOp",EDGE,"E64");var subQ1=sQuery(id+"F0.wireOp",EDGE,"E37");var subQ2=makeQuery(id+"F0.imprint","INTERSECT",VERTEX,{"derivedFrom":[subQ1,subQ0]});Q0=makeQuery(id+"F0.imprint","IMPRINT",FACE,{"disambiguationData":[TD([[makeQuery(id+"F0.imprint","IMPRINT",EDGE,{"disambiguationData":[TD([[subQ2,1.0]])],"derivedFrom":subQ1}),1.0]])]});}
            var Q1;
            {var subQ0=sQuery(id+"F0.wireOp",EDGE,"E64");var subQ1=sQuery(id+"F0.wireOp",EDGE,"E39");var subQ2=makeQuery(id+"F0.imprint","INTERSECT",VERTEX,{"derivedFrom":[subQ1,subQ0]});Q1=makeQuery(id+"F0.imprint","IMPRINT",FACE,{"disambiguationData":[TD([[makeQuery(id+"F0.imprint","IMPRINT",EDGE,{"disambiguationData":[TD([[subQ2,-1.0]])],"derivedFrom":subQ1}),1.0]])]});}
            var Q2;
            {var subQ0=sQuery(id+"F0.wireOp",EDGE,"E65");var subQ1=sQuery(id+"F0.wireOp",EDGE,"E36");var subQ2=makeQuery(id+"F0.imprint","INTERSECT",VERTEX,{"derivedFrom":[subQ1,subQ0]});Q2=makeQuery(id+"F0.imprint","IMPRINT",FACE,{"disambiguationData":[TD([[makeQuery(id+"F0.imprint","IMPRINT",EDGE,{"disambiguationData":[TD([[subQ2,-1.0]])],"derivedFrom":subQ1}),1.0]])]});}
            var Q3;
            {var subQ0=sQuery(id+"F0.wireOp",EDGE,"E65");var subQ1=sQuery(id+"F0.wireOp",EDGE,"E38");var subQ2=makeQuery(id+"F0.imprint","INTERSECT",VERTEX,{"derivedFrom":[subQ1,subQ0]});Q3=makeQuery(id+"F0.imprint","IMPRINT",FACE,{"disambiguationData":[TD([[makeQuery(id+"F0.imprint","IMPRINT",EDGE,{"disambiguationData":[TD([[subQ2,1.0]])],"derivedFrom":subQ1}),1.0]])]});}
            var Q4;
            {var subQ0=sQuery(id+"F0.wireOp",EDGE,"E66");var subQ1=sQuery(id+"F0.wireOp",EDGE,"E35");var subQ2=makeQuery(id+"F0.imprint","INTERSECT",VERTEX,{"derivedFrom":[subQ1,subQ0]});Q4=makeQuery(id+"F0.imprint","IMPRINT",FACE,{"disambiguationData":[TD([[makeQuery(id+"F0.imprint","IMPRINT",EDGE,{"disambiguationData":[TD([[subQ2,-1.0]])],"derivedFrom":subQ1}),-1.0]])]});}
            var Q5;
            {var subQ0=sQuery(id+"F0.wireOp",EDGE,"E126");var subQ1=sQuery(id+"F0.wireOp",EDGE,"E34");var subQ2=makeQuery(id+"F0.imprint","INTERSECT",VERTEX,{"derivedFrom":[subQ1,subQ0]});Q5=makeQuery(id+"F0.imprint","IMPRINT",FACE,{"disambiguationData":[TD([[makeQuery(id+"F0.imprint","IMPRINT",EDGE,{"disambiguationData":[TD([[subQ2,-1.0]])],"derivedFrom":subQ1}),-1.0]])]});}
            var Q6;
            {var subQ0=sQuery(id+"F0.wireOp",EDGE,"E126");var subQ1=sQuery(id+"F0.wireOp",EDGE,"E32");var subQ2=makeQuery(id+"F0.imprint","INTERSECT",VERTEX,{"derivedFrom":[subQ1,subQ0]});Q6=makeQuery(id+"F0.imprint","IMPRINT",FACE,{"disambiguationData":[TD([[makeQuery(id+"F0.imprint","IMPRINT",EDGE,{"disambiguationData":[TD([[subQ2,1.0]])],"derivedFrom":subQ1}),-1.0]])]});}
            var Q7;
            {var subQ0=sQuery(id+"F0.wireOp",EDGE,"E66");var subQ1=sQuery(id+"F0.wireOp",EDGE,"E33");var subQ2=makeQuery(id+"F0.imprint","INTERSECT",VERTEX,{"derivedFrom":[subQ1,subQ0]});Q7=makeQuery(id+"F0.imprint","IMPRINT",FACE,{"disambiguationData":[TD([[makeQuery(id+"F0.imprint","IMPRINT",EDGE,{"disambiguationData":[TD([[subQ2,1.0]])],"derivedFrom":subQ1}),-1.0]])]});}
            var Q8;
            {var subQ0=sQuery(id+"F0.wireOp",EDGE,"E70");var subQ1=sQuery(id+"F0.wireOp",EDGE,"E47");var subQ2=makeQuery(id+"F0.imprint","INTERSECT",VERTEX,{"derivedFrom":[subQ1,subQ0]});Q8=makeQuery(id+"F0.imprint","IMPRINT",FACE,{"disambiguationData":[TD([[makeQuery(id+"F0.imprint","IMPRINT",EDGE,{"disambiguationData":[TD([[subQ2,1.0]])],"derivedFrom":subQ1}),1.0]])]});}
            var Q9;
            {var subQ0=sQuery(id+"F0.wireOp",EDGE,"E71");var subQ1=sQuery(id+"F0.wireOp",EDGE,"E44");var subQ2=makeQuery(id+"F0.imprint","INTERSECT",VERTEX,{"derivedFrom":[subQ1,subQ0]});Q9=makeQuery(id+"F0.imprint","IMPRINT",FACE,{"disambiguationData":[TD([[makeQuery(id+"F0.imprint","IMPRINT",EDGE,{"disambiguationData":[TD([[subQ2,1.0]])],"derivedFrom":subQ1}),1.0]])]});}
            var Q10;
            {var subQ0=sQuery(id+"F0.wireOp",EDGE,"E71");var subQ1=sQuery(id+"F0.wireOp",EDGE,"E46");var subQ2=makeQuery(id+"F0.imprint","INTERSECT",VERTEX,{"derivedFrom":[subQ1,subQ0]});Q10=makeQuery(id+"F0.imprint","IMPRINT",FACE,{"disambiguationData":[TD([[makeQuery(id+"F0.imprint","IMPRINT",EDGE,{"disambiguationData":[TD([[subQ2,-1.0]])],"derivedFrom":subQ1}),1.0]])]});}
            var Q11;
            {var subQ0=sQuery(id+"F0.wireOp",EDGE,"E70");var subQ1=sQuery(id+"F0.wireOp",EDGE,"E45");var subQ2=makeQuery(id+"F0.imprint","INTERSECT",VERTEX,{"derivedFrom":[subQ1,subQ0]});Q11=makeQuery(id+"F0.imprint","IMPRINT",FACE,{"disambiguationData":[TD([[makeQuery(id+"F0.imprint","IMPRINT",EDGE,{"disambiguationData":[TD([[subQ2,-1.0]])],"derivedFrom":subQ1}),1.0]])]});}
            var Q12;
            {var subQ0=sQuery(id+"F0.wireOp",EDGE,"E72");var subQ1=sQuery(id+"F0.wireOp",EDGE,"E43");var subQ2=makeQuery(id+"F0.imprint","INTERSECT",VERTEX,{"derivedFrom":[subQ1,subQ0]});Q12=makeQuery(id+"F0.imprint","IMPRINT",FACE,{"disambiguationData":[TD([[makeQuery(id+"F0.imprint","IMPRINT",EDGE,{"disambiguationData":[TD([[subQ2,-1.0]])],"derivedFrom":subQ1}),-1.0]])]});}
            var Q13;
            {var subQ0=sQuery(id+"F0.wireOp",EDGE,"E73");var subQ1=sQuery(id+"F0.wireOp",EDGE,"E42");var subQ2=makeQuery(id+"F0.imprint","INTERSECT",VERTEX,{"derivedFrom":[subQ1,subQ0]});Q13=makeQuery(id+"F0.imprint","IMPRINT",FACE,{"disambiguationData":[TD([[makeQuery(id+"F0.imprint","IMPRINT",EDGE,{"disambiguationData":[TD([[subQ2,-1.0]])],"derivedFrom":subQ1}),-1.0]])]});}
            var Q14;
            {var subQ0=sQuery(id+"F0.wireOp",EDGE,"E73");var subQ1=sQuery(id+"F0.wireOp",EDGE,"E40");var subQ2=makeQuery(id+"F0.imprint","INTERSECT",VERTEX,{"derivedFrom":[subQ1,subQ0]});Q14=makeQuery(id+"F0.imprint","IMPRINT",FACE,{"disambiguationData":[TD([[makeQuery(id+"F0.imprint","IMPRINT",EDGE,{"disambiguationData":[TD([[subQ2,1.0]])],"derivedFrom":subQ1}),-1.0]])]});}
            var Q15;
            {var subQ0=sQuery(id+"F0.wireOp",EDGE,"E72");var subQ1=sQuery(id+"F0.wireOp",EDGE,"E41");var subQ2=makeQuery(id+"F0.imprint","INTERSECT",VERTEX,{"derivedFrom":[subQ1,subQ0]});Q15=makeQuery(id+"F0.imprint","IMPRINT",FACE,{"disambiguationData":[TD([[makeQuery(id+"F0.imprint","IMPRINT",EDGE,{"disambiguationData":[TD([[subQ2,1.0]])],"derivedFrom":subQ1}),-1.0]])]});}
            var Q16;
            {var subQ0=sQuery(id+"F0.wireOp",EDGE,"E68");var subQ1=sQuery(id+"F0.wireOp",EDGE,"E2");var subQ2=makeQuery(id+"F0.imprint","INTERSECT",VERTEX,{"derivedFrom":[subQ1,subQ0]});Q16=makeQuery(id+"F0.imprint","IMPRINT",FACE,{"disambiguationData":[TD([[makeQuery(id+"F0.imprint","IMPRINT",EDGE,{"disambiguationData":[TD([[subQ2,-1.0]])],"derivedFrom":subQ1}),-1.0]])]});}
            var Q17;
            {var subQ0=sQuery(id+"F0.wireOp",EDGE,"E17");var subQ1=sQuery(id+"F0.wireOp",EDGE,"E1");var subQ2=makeQuery(id+"F0.imprint","INTERSECT",VERTEX,{"derivedFrom":[subQ1,subQ0]});Q17=makeQuery(id+"F0.imprint","IMPRINT",FACE,{"disambiguationData":[TD([[makeQuery(id+"F0.imprint","IMPRINT",EDGE,{"disambiguationData":[TD([[subQ2,1.0]])],"derivedFrom":subQ1}),1.0]])]});}
            var Q18;
            {var subQ0=sQuery(id+"F0.wireOp",EDGE,"E17");var subQ1=sQuery(id+"F0.wireOp",EDGE,"E3");var subQ2=makeQuery(id+"F0.imprint","INTERSECT",VERTEX,{"derivedFrom":[subQ1,subQ0]});Q18=makeQuery(id+"F0.imprint","IMPRINT",FACE,{"disambiguationData":[TD([[makeQuery(id+"F0.imprint","IMPRINT",EDGE,{"disambiguationData":[TD([[subQ2,1.0]])],"derivedFrom":subQ1}),-1.0]])]});}
            var Q19;
            {var subQ0=sQuery(id+"F0.wireOp",EDGE,"E68");var subQ1=sQuery(id+"F0.wireOp",EDGE,"E4");var subQ2=makeQuery(id+"F0.imprint","INTERSECT",VERTEX,{"derivedFrom":[subQ1,subQ0]});Q19=makeQuery(id+"F0.imprint","IMPRINT",FACE,{"disambiguationData":[TD([[makeQuery(id+"F0.imprint","IMPRINT",EDGE,{"disambiguationData":[TD([[subQ2,-1.0]])],"derivedFrom":subQ1}),1.0]])]});}
            var Q20;
            {var subQ0=sQuery(id+"F0.wireOp",EDGE,"E69");var subQ1=sQuery(id+"F0.wireOp",EDGE,"E23");var subQ2=makeQuery(id+"F0.imprint","INTERSECT",VERTEX,{"derivedFrom":[subQ1,subQ0]});Q20=makeQuery(id+"F0.imprint","IMPRINT",FACE,{"disambiguationData":[TD([[makeQuery(id+"F0.imprint","IMPRINT",EDGE,{"disambiguationData":[TD([[subQ2,-1.0]])],"derivedFrom":subQ1}),-1.0]])]});}
            var Q21;
            {var subQ0=sQuery(id+"F0.wireOp",EDGE,"E69");var subQ1=sQuery(id+"F0.wireOp",EDGE,"E25");var subQ2=makeQuery(id+"F0.imprint","INTERSECT",VERTEX,{"derivedFrom":[subQ1,subQ0]});Q21=makeQuery(id+"F0.imprint","IMPRINT",FACE,{"disambiguationData":[TD([[makeQuery(id+"F0.imprint","IMPRINT",EDGE,{"disambiguationData":[TD([[subQ2,-1.0]])],"derivedFrom":subQ1}),1.0]])]});}
            var Q22;
            {var subQ0=sQuery(id+"F0.wireOp",EDGE,"E26");var subQ1=sQuery(id+"F0.wireOp",EDGE,"E24");var subQ2=makeQuery(id+"F0.imprint","INTERSECT",VERTEX,{"derivedFrom":[subQ1,subQ0]});Q22=makeQuery(id+"F0.imprint","IMPRINT",FACE,{"disambiguationData":[TD([[makeQuery(id+"F0.imprint","IMPRINT",EDGE,{"disambiguationData":[TD([[subQ2,1.0]])],"derivedFrom":subQ1}),-1.0]])]});}
            var Q23;
            {var subQ0=sQuery(id+"F0.wireOp",EDGE,"E68");var subQ1=sQuery(id+"F0.wireOp",EDGE,"E17");var subQ2=makeQuery(id+"F0.imprint","INTERSECT",VERTEX,{"derivedFrom":[subQ1,subQ0]});Q23=makeQuery(id+"F0.imprint","IMPRINT",FACE,{"disambiguationData":[TD([[makeQuery(id+"F0.imprint","IMPRINT",EDGE,{"disambiguationData":[TD([[subQ2,-1.0]])],"derivedFrom":subQ1}),1.0]])]});}
            var Q24;
            {var subQ0=sQuery(id+"F0.wireOp",EDGE,"E26");var subQ1=sQuery(id+"F0.wireOp",EDGE,"E22");var subQ2=makeQuery(id+"F0.imprint","INTERSECT",VERTEX,{"derivedFrom":[subQ1,subQ0]});Q24=makeQuery(id+"F0.imprint","IMPRINT",FACE,{"disambiguationData":[TD([[makeQuery(id+"F0.imprint","IMPRINT",EDGE,{"disambiguationData":[TD([[subQ2,1.0]])],"derivedFrom":subQ1}),1.0]])]});}
            var Q25;
            {var subQ0=sQuery(id+"F0.wireOp",EDGE,"E69");var subQ1=sQuery(id+"F0.wireOp",EDGE,"E26");var subQ2=makeQuery(id+"F0.imprint","INTERSECT",VERTEX,{"derivedFrom":[subQ1,subQ0]});Q25=makeQuery(id+"F0.imprint","IMPRINT",FACE,{"disambiguationData":[TD([[makeQuery(id+"F0.imprint","IMPRINT",EDGE,{"disambiguationData":[TD([[subQ2,-1.0]])],"derivedFrom":subQ1}),1.0]])]});}
            var Q26;
            {var subQ0=sQuery(id+"F0.wireOp",EDGE,"E127");var subQ1=sQuery(id+"F0.wireOp",EDGE,"E66");var subQ2=makeQuery(id+"F0.imprint","INTERSECT",VERTEX,{"derivedFrom":[subQ1,subQ0]});Q26=makeQuery(id+"F0.imprint","IMPRINT",FACE,{"disambiguationData":[TD([[makeQuery(id+"F0.imprint","IMPRINT",EDGE,{"disambiguationData":[TD([[subQ2,-1.0]])],"derivedFrom":subQ1}),1.0]])]});}
            var Q27;
            {var subQ0=sQuery(id+"F0.wireOp",EDGE,"E125");var subQ1=sQuery(id+"F0.wireOp",EDGE,"E64");var subQ2=makeQuery(id+"F0.imprint","INTERSECT",VERTEX,{"derivedFrom":[subQ1,subQ0]});Q27=makeQuery(id+"F0.imprint","IMPRINT",FACE,{"disambiguationData":[TD([[makeQuery(id+"F0.imprint","IMPRINT",EDGE,{"disambiguationData":[TD([[subQ2,-1.0]])],"derivedFrom":subQ1}),1.0]])]});}
            var Q28;
            {var subQ0=sQuery(id+"F0.wireOp",EDGE,"E131");var subQ1=sQuery(id+"F0.wireOp",EDGE,"E70");var subQ2=makeQuery(id+"F0.imprint","INTERSECT",VERTEX,{"derivedFrom":[subQ1,subQ0]});Q28=makeQuery(id+"F0.imprint","IMPRINT",FACE,{"disambiguationData":[TD([[makeQuery(id+"F0.imprint","IMPRINT",EDGE,{"disambiguationData":[TD([[subQ2,-1.0]])],"derivedFrom":subQ1}),1.0]])]});}
            var Q29;
            {var subQ0=sQuery(id+"F0.wireOp",EDGE,"E132");var subQ1=sQuery(id+"F0.wireOp",EDGE,"E72");var subQ2=makeQuery(id+"F0.imprint","INTERSECT",VERTEX,{"derivedFrom":[subQ1,subQ0]});Q29=makeQuery(id+"F0.imprint","IMPRINT",FACE,{"disambiguationData":[TD([[makeQuery(id+"F0.imprint","IMPRINT",EDGE,{"disambiguationData":[TD([[subQ2,-1.0]])],"derivedFrom":subQ1}),1.0]])]});}
            var Q30;
            {var subQ0=sQuery(id+"F0.wireOp",EDGE,"E95");var subQ1=sQuery(id+"F0.wireOp",EDGE,"E6");var subQ2=makeQuery(id+"F0.imprint","INTERSECT",VERTEX,{"derivedFrom":[subQ1,subQ0]});Q30=makeQuery(id+"F0.imprint","IMPRINT",FACE,{"disambiguationData":[TD([[makeQuery(id+"F0.imprint","IMPRINT",EDGE,{"disambiguationData":[TD([[subQ2,-1.0]])],"derivedFrom":subQ1}),-1.0]])]});}
            var Q31;
            {var subQ0=sQuery(id+"F0.wireOp",EDGE,"E18");var subQ1=sQuery(id+"F0.wireOp",EDGE,"E5");var subQ2=makeQuery(id+"F0.imprint","INTERSECT",VERTEX,{"derivedFrom":[subQ1,subQ0]});Q31=makeQuery(id+"F0.imprint","IMPRINT",FACE,{"disambiguationData":[TD([[makeQuery(id+"F0.imprint","IMPRINT",EDGE,{"disambiguationData":[TD([[subQ2,1.0]])],"derivedFrom":subQ1}),1.0]])]});}
            var Q32;
            {var subQ0=sQuery(id+"F0.wireOp",EDGE,"E18");var subQ1=sQuery(id+"F0.wireOp",EDGE,"E7");var subQ2=makeQuery(id+"F0.imprint","INTERSECT",VERTEX,{"derivedFrom":[subQ1,subQ0]});Q32=makeQuery(id+"F0.imprint","IMPRINT",FACE,{"disambiguationData":[TD([[makeQuery(id+"F0.imprint","IMPRINT",EDGE,{"disambiguationData":[TD([[subQ2,1.0]])],"derivedFrom":subQ1}),-1.0]])]});}
            var Q33;
            {var subQ0=sQuery(id+"F0.wireOp",EDGE,"E95");var subQ1=sQuery(id+"F0.wireOp",EDGE,"E8");var subQ2=makeQuery(id+"F0.imprint","INTERSECT",VERTEX,{"derivedFrom":[subQ1,subQ0]});Q33=makeQuery(id+"F0.imprint","IMPRINT",FACE,{"disambiguationData":[TD([[makeQuery(id+"F0.imprint","IMPRINT",EDGE,{"disambiguationData":[TD([[subQ2,-1.0]])],"derivedFrom":subQ1}),1.0]])]});}
            var Q34;
            {var subQ0=sQuery(id+"F0.wireOp",EDGE,"E95");var subQ1=sQuery(id+"F0.wireOp",EDGE,"E18");var subQ2=makeQuery(id+"F0.imprint","INTERSECT",VERTEX,{"derivedFrom":[subQ1,subQ0]});Q34=makeQuery(id+"F0.imprint","IMPRINT",FACE,{"disambiguationData":[TD([[makeQuery(id+"F0.imprint","IMPRINT",EDGE,{"disambiguationData":[TD([[subQ2,-1.0]])],"derivedFrom":subQ1}),1.0]])]});}
            var Q35;
            {var subQ0=sQuery(id+"F0.wireOp",EDGE,"E96");var subQ1=sQuery(id+"F0.wireOp",EDGE,"E28");var subQ2=makeQuery(id+"F0.imprint","INTERSECT",VERTEX,{"derivedFrom":[subQ1,subQ0]});Q35=makeQuery(id+"F0.imprint","IMPRINT",FACE,{"disambiguationData":[TD([[makeQuery(id+"F0.imprint","IMPRINT",EDGE,{"disambiguationData":[TD([[subQ2,-1.0]])],"derivedFrom":subQ1}),-1.0]])]});}
            var Q36;
            {var subQ0=sQuery(id+"F0.wireOp",EDGE,"E31");var subQ1=sQuery(id+"F0.wireOp",EDGE,"E27");var subQ2=makeQuery(id+"F0.imprint","INTERSECT",VERTEX,{"derivedFrom":[subQ1,subQ0]});Q36=makeQuery(id+"F0.imprint","IMPRINT",FACE,{"disambiguationData":[TD([[makeQuery(id+"F0.imprint","IMPRINT",EDGE,{"disambiguationData":[TD([[subQ2,1.0]])],"derivedFrom":subQ1}),1.0]])]});}
            var Q37;
            {var subQ0=sQuery(id+"F0.wireOp",EDGE,"E31");var subQ1=sQuery(id+"F0.wireOp",EDGE,"E29");var subQ2=makeQuery(id+"F0.imprint","INTERSECT",VERTEX,{"derivedFrom":[subQ1,subQ0]});Q37=makeQuery(id+"F0.imprint","IMPRINT",FACE,{"disambiguationData":[TD([[makeQuery(id+"F0.imprint","IMPRINT",EDGE,{"disambiguationData":[TD([[subQ2,1.0]])],"derivedFrom":subQ1}),-1.0]])]});}
            var Q38;
            {var subQ0=sQuery(id+"F0.wireOp",EDGE,"E96");var subQ1=sQuery(id+"F0.wireOp",EDGE,"E30");var subQ2=makeQuery(id+"F0.imprint","INTERSECT",VERTEX,{"derivedFrom":[subQ1,subQ0]});Q38=makeQuery(id+"F0.imprint","IMPRINT",FACE,{"disambiguationData":[TD([[makeQuery(id+"F0.imprint","IMPRINT",EDGE,{"disambiguationData":[TD([[subQ2,1.0]])],"derivedFrom":subQ1}),-1.0]])]});}
            var Q39;
            {var subQ0=sQuery(id+"F0.wireOp",EDGE,"E96");var subQ1=sQuery(id+"F0.wireOp",EDGE,"E31");var subQ2=makeQuery(id+"F0.imprint","INTERSECT",VERTEX,{"derivedFrom":[subQ1,subQ0]});Q39=makeQuery(id+"F0.imprint","IMPRINT",FACE,{"disambiguationData":[TD([[makeQuery(id+"F0.imprint","IMPRINT",EDGE,{"disambiguationData":[TD([[subQ2,-1.0]])],"derivedFrom":subQ1}),1.0]])]});}
            var Q40;
            {var subQ0=sQuery(id+"F0.wireOp",EDGE,"E107");var subQ1=sQuery(id+"F0.wireOp",EDGE,"E97.top");var subQ2=makeQuery(id+"F0.imprint","INTERSECT",VERTEX,{"derivedFrom":[subQ1,subQ0]});Q40=makeQuery(id+"F0.imprint","IMPRINT",FACE,{"disambiguationData":[TD([[makeQuery(id+"F0.imprint","IMPRINT",EDGE,{"disambiguationData":[TD([[subQ2,-1.0]])],"derivedFrom":subQ1}),-1.0]])]});}
            var Q41;
            {var subQ0=sQuery(id+"F0.wireOp",EDGE,"E108");var subQ1=sQuery(id+"F0.wireOp",EDGE,"E97.left");var subQ2=makeQuery(id+"F0.imprint","INTERSECT",VERTEX,{"derivedFrom":[subQ1,subQ0]});Q41=makeQuery(id+"F0.imprint","IMPRINT",FACE,{"disambiguationData":[TD([[makeQuery(id+"F0.imprint","IMPRINT",EDGE,{"disambiguationData":[TD([[subQ2,-1.0]])],"derivedFrom":subQ1}),-1.0]])]});}
            var Q42;
            {var subQ0=sQuery(id+"F0.wireOp",EDGE,"E130");var subQ1=sQuery(id+"F0.wireOp",EDGE,"E107");var subQ2=makeQuery(id+"F0.imprint","INTERSECT",VERTEX,{"derivedFrom":[subQ1,subQ0]});Q42=makeQuery(id+"F0.imprint","IMPRINT",FACE,{"disambiguationData":[TD([[makeQuery(id+"F0.imprint","IMPRINT",EDGE,{"disambiguationData":[TD([[subQ2,-1.0]])],"derivedFrom":subQ1}),1.0]])]});}
            var Q43;
            {var subQ0=sQuery(id+"F0.wireOp",EDGE,"E108");var subQ1=sQuery(id+"F0.wireOp",EDGE,"E97.right");var subQ2=makeQuery(id+"F0.imprint","INTERSECT",VERTEX,{"derivedFrom":[subQ1,subQ0]});Q43=makeQuery(id+"F0.imprint","IMPRINT",FACE,{"disambiguationData":[TD([[makeQuery(id+"F0.imprint","IMPRINT",EDGE,{"disambiguationData":[TD([[subQ2,-1.0]])],"derivedFrom":subQ1}),1.0]])]});}
            var Q44;
            {var subQ0=sQuery(id+"F0.wireOp",EDGE,"E107");var subQ1=sQuery(id+"F0.wireOp",EDGE,"E97.bottom");var subQ2=makeQuery(id+"F0.imprint","INTERSECT",VERTEX,{"derivedFrom":[subQ1,subQ0]});Q44=makeQuery(id+"F0.imprint","IMPRINT",FACE,{"disambiguationData":[TD([[makeQuery(id+"F0.imprint","IMPRINT",EDGE,{"disambiguationData":[TD([[subQ2,-1.0]])],"derivedFrom":subQ1}),1.0]])]});}
            var Q45;
            {var subQ0=sQuery(id+"F0.wireOp",EDGE,"E109");var subQ1=sQuery(id+"F0.wireOp",EDGE,"E100.top");var subQ2=makeQuery(id+"F0.imprint","INTERSECT",VERTEX,{"derivedFrom":[subQ1,subQ0]});Q45=makeQuery(id+"F0.imprint","IMPRINT",FACE,{"disambiguationData":[TD([[makeQuery(id+"F0.imprint","IMPRINT",EDGE,{"disambiguationData":[TD([[subQ2,-1.0]])],"derivedFrom":subQ1}),-1.0]])]});}
            var Q46;
            {var subQ0=sQuery(id+"F0.wireOp",EDGE,"E110");var subQ1=sQuery(id+"F0.wireOp",EDGE,"E100.left");var subQ2=makeQuery(id+"F0.imprint","INTERSECT",VERTEX,{"derivedFrom":[subQ1,subQ0]});Q46=makeQuery(id+"F0.imprint","IMPRINT",FACE,{"disambiguationData":[TD([[makeQuery(id+"F0.imprint","IMPRINT",EDGE,{"disambiguationData":[TD([[subQ2,-1.0]])],"derivedFrom":subQ1}),-1.0]])]});}
            var Q47;
            {var subQ0=sQuery(id+"F0.wireOp",EDGE,"E135");var subQ1=sQuery(id+"F0.wireOp",EDGE,"E109");var subQ2=makeQuery(id+"F0.imprint","INTERSECT",VERTEX,{"derivedFrom":[subQ1,subQ0]});Q47=makeQuery(id+"F0.imprint","IMPRINT",FACE,{"disambiguationData":[TD([[makeQuery(id+"F0.imprint","IMPRINT",EDGE,{"disambiguationData":[TD([[subQ2,-1.0]])],"derivedFrom":subQ1}),1.0]])]});}
            var Q48;
            {var subQ0=sQuery(id+"F0.wireOp",EDGE,"E110");var subQ1=sQuery(id+"F0.wireOp",EDGE,"E100.right");var subQ2=makeQuery(id+"F0.imprint","INTERSECT",VERTEX,{"derivedFrom":[subQ1,subQ0]});Q48=makeQuery(id+"F0.imprint","IMPRINT",FACE,{"disambiguationData":[TD([[makeQuery(id+"F0.imprint","IMPRINT",EDGE,{"disambiguationData":[TD([[subQ2,-1.0]])],"derivedFrom":subQ1}),1.0]])]});}
            var Q49;
            {var subQ0=sQuery(id+"F0.wireOp",EDGE,"E109");var subQ1=sQuery(id+"F0.wireOp",EDGE,"E100.bottom");var subQ2=makeQuery(id+"F0.imprint","INTERSECT",VERTEX,{"derivedFrom":[subQ1,subQ0]});Q49=makeQuery(id+"F0.imprint","IMPRINT",FACE,{"disambiguationData":[TD([[makeQuery(id+"F0.imprint","IMPRINT",EDGE,{"disambiguationData":[TD([[subQ2,-1.0]])],"derivedFrom":subQ1}),1.0]])]});}
            var Q50;
            {var subQ0=sQuery(id+"F0.wireOp",EDGE,"E106");var subQ1=sQuery(id+"F0.wireOp",EDGE,"E98.bottom");var subQ2=makeQuery(id+"F0.imprint","INTERSECT",VERTEX,{"derivedFrom":[subQ1,subQ0]});Q50=makeQuery(id+"F0.imprint","IMPRINT",FACE,{"disambiguationData":[TD([[makeQuery(id+"F0.imprint","IMPRINT",EDGE,{"disambiguationData":[TD([[subQ2,-1.0]])],"derivedFrom":subQ1}),-1.0]])]});}
            var Q51;
            {var subQ0=sQuery(id+"F0.wireOp",EDGE,"E105");var subQ1=sQuery(id+"F0.wireOp",EDGE,"E98.left");var subQ2=makeQuery(id+"F0.imprint","INTERSECT",VERTEX,{"derivedFrom":[subQ1,subQ0]});Q51=makeQuery(id+"F0.imprint","IMPRINT",FACE,{"disambiguationData":[TD([[makeQuery(id+"F0.imprint","IMPRINT",EDGE,{"disambiguationData":[TD([[subQ2,-1.0]])],"derivedFrom":subQ1}),1.0]])]});}
            var Q52;
            {var subQ0=sQuery(id+"F0.wireOp",EDGE,"E106");var subQ1=sQuery(id+"F0.wireOp",EDGE,"E105");var subQ2=makeQuery(id+"F0.imprint","INTERSECT",VERTEX,{"derivedFrom":[subQ1,subQ0]});Q52=makeQuery(id+"F0.imprint","IMPRINT",FACE,{"disambiguationData":[TD([[makeQuery(id+"F0.imprint","IMPRINT",EDGE,{"disambiguationData":[TD([[subQ2,-1.0]])],"derivedFrom":subQ1}),-1.0]])]});}
            var Q53;
            {var subQ0=sQuery(id+"F0.wireOp",EDGE,"E105");var subQ1=sQuery(id+"F0.wireOp",EDGE,"E98.right");var subQ2=makeQuery(id+"F0.imprint","INTERSECT",VERTEX,{"derivedFrom":[subQ1,subQ0]});Q53=makeQuery(id+"F0.imprint","IMPRINT",FACE,{"disambiguationData":[TD([[makeQuery(id+"F0.imprint","IMPRINT",EDGE,{"disambiguationData":[TD([[subQ2,-1.0]])],"derivedFrom":subQ1}),-1.0]])]});}
            var Q54;
            {var subQ0=sQuery(id+"F0.wireOp",EDGE,"E106");var subQ1=sQuery(id+"F0.wireOp",EDGE,"E98.top");var subQ2=makeQuery(id+"F0.imprint","INTERSECT",VERTEX,{"derivedFrom":[subQ1,subQ0]});Q54=makeQuery(id+"F0.imprint","IMPRINT",FACE,{"disambiguationData":[TD([[makeQuery(id+"F0.imprint","IMPRINT",EDGE,{"disambiguationData":[TD([[subQ2,-1.0]])],"derivedFrom":subQ1}),1.0]])]});}
            var Q55;
            {var subQ0=sQuery(id+"F0.wireOp",EDGE,"E111");var subQ1=sQuery(id+"F0.wireOp",EDGE,"E99.bottom");var subQ2=makeQuery(id+"F0.imprint","INTERSECT",VERTEX,{"derivedFrom":[subQ1,subQ0]});Q55=makeQuery(id+"F0.imprint","IMPRINT",FACE,{"disambiguationData":[TD([[makeQuery(id+"F0.imprint","IMPRINT",EDGE,{"disambiguationData":[TD([[subQ2,-1.0]])],"derivedFrom":subQ1}),-1.0]])]});}
            var Q56;
            {var subQ0=sQuery(id+"F0.wireOp",EDGE,"E112");var subQ1=sQuery(id+"F0.wireOp",EDGE,"E111");var subQ2=makeQuery(id+"F0.imprint","INTERSECT",VERTEX,{"derivedFrom":[subQ1,subQ0]});Q56=makeQuery(id+"F0.imprint","IMPRINT",FACE,{"disambiguationData":[TD([[makeQuery(id+"F0.imprint","IMPRINT",EDGE,{"disambiguationData":[TD([[subQ2,-1.0]])],"derivedFrom":subQ1}),1.0]])]});}
            var Q57;
            {var subQ0=sQuery(id+"F0.wireOp",EDGE,"E111");var subQ1=sQuery(id+"F0.wireOp",EDGE,"E99.top");var subQ2=makeQuery(id+"F0.imprint","INTERSECT",VERTEX,{"derivedFrom":[subQ1,subQ0]});Q57=makeQuery(id+"F0.imprint","IMPRINT",FACE,{"disambiguationData":[TD([[makeQuery(id+"F0.imprint","IMPRINT",EDGE,{"disambiguationData":[TD([[subQ2,-1.0]])],"derivedFrom":subQ1}),1.0]])]});}
            var Q58;
            {var subQ0=sQuery(id+"F0.wireOp",EDGE,"E112");var subQ1=sQuery(id+"F0.wireOp",EDGE,"E99.left");var subQ2=makeQuery(id+"F0.imprint","INTERSECT",VERTEX,{"derivedFrom":[subQ1,subQ0]});Q58=makeQuery(id+"F0.imprint","IMPRINT",FACE,{"disambiguationData":[TD([[makeQuery(id+"F0.imprint","IMPRINT",EDGE,{"disambiguationData":[TD([[subQ2,-1.0]])],"derivedFrom":subQ1}),1.0]])]});}
            var Q59;
            {var subQ0=sQuery(id+"F0.wireOp",EDGE,"E112");var subQ1=sQuery(id+"F0.wireOp",EDGE,"E99.right");var subQ2=makeQuery(id+"F0.imprint","INTERSECT",VERTEX,{"derivedFrom":[subQ1,subQ0]});Q59=makeQuery(id+"F0.imprint","IMPRINT",FACE,{"disambiguationData":[TD([[makeQuery(id+"F0.imprint","IMPRINT",EDGE,{"disambiguationData":[TD([[subQ2,-1.0]])],"derivedFrom":subQ1}),-1.0]])]});}
            var Q60;
            {var subQ0=sQuery(id+"F0.wireOp",EDGE,"E113");var subQ1=sQuery(id+"F0.wireOp",EDGE,"E101.bottom");var subQ2=makeQuery(id+"F0.imprint","INTERSECT",VERTEX,{"derivedFrom":[subQ1,subQ0]});Q60=makeQuery(id+"F0.imprint","IMPRINT",FACE,{"disambiguationData":[TD([[makeQuery(id+"F0.imprint","IMPRINT",EDGE,{"disambiguationData":[TD([[subQ2,-1.0]])],"derivedFrom":subQ1}),-1.0]])]});}
            var Q61;
            {var subQ0=sQuery(id+"F0.wireOp",EDGE,"E113");var subQ1=sQuery(id+"F0.wireOp",EDGE,"E101.top");var subQ2=makeQuery(id+"F0.imprint","INTERSECT",VERTEX,{"derivedFrom":[subQ1,subQ0]});Q61=makeQuery(id+"F0.imprint","IMPRINT",FACE,{"disambiguationData":[TD([[makeQuery(id+"F0.imprint","IMPRINT",EDGE,{"disambiguationData":[TD([[subQ2,-1.0]])],"derivedFrom":subQ1}),1.0]])]});}
            var Q62;
            {var subQ0=sQuery(id+"F0.wireOp",EDGE,"E114");var subQ1=sQuery(id+"F0.wireOp",EDGE,"E101.left");var subQ2=makeQuery(id+"F0.imprint","INTERSECT",VERTEX,{"derivedFrom":[subQ1,subQ0]});Q62=makeQuery(id+"F0.imprint","IMPRINT",FACE,{"disambiguationData":[TD([[makeQuery(id+"F0.imprint","IMPRINT",EDGE,{"disambiguationData":[TD([[subQ2,-1.0]])],"derivedFrom":subQ1}),1.0]])]});}
            var Q63;
            {var subQ0=sQuery(id+"F0.wireOp",EDGE,"E114");var subQ1=sQuery(id+"F0.wireOp",EDGE,"E101.right");var subQ2=makeQuery(id+"F0.imprint","INTERSECT",VERTEX,{"derivedFrom":[subQ1,subQ0]});Q63=makeQuery(id+"F0.imprint","IMPRINT",FACE,{"disambiguationData":[TD([[makeQuery(id+"F0.imprint","IMPRINT",EDGE,{"disambiguationData":[TD([[subQ2,-1.0]])],"derivedFrom":subQ1}),-1.0]])]});}
            var Q64;
            {var subQ0=sQuery(id+"F0.wireOp",EDGE,"E114");var subQ1=sQuery(id+"F0.wireOp",EDGE,"E113");var subQ2=makeQuery(id+"F0.imprint","INTERSECT",VERTEX,{"derivedFrom":[subQ1,subQ0]});Q64=makeQuery(id+"F0.imprint","IMPRINT",FACE,{"disambiguationData":[TD([[makeQuery(id+"F0.imprint","IMPRINT",EDGE,{"disambiguationData":[TD([[subQ2,-1.0]])],"derivedFrom":subQ1}),1.0]])]});}
            var Q65;
            {var subQ0=sQuery(id+"F0.wireOp",EDGE,"E82");var subQ1=sQuery(id+"F0.wireOp",EDGE,"E10");var subQ2=makeQuery(id+"F0.imprint","INTERSECT",VERTEX,{"derivedFrom":[subQ1,subQ0]});Q65=makeQuery(id+"F0.imprint","IMPRINT",FACE,{"disambiguationData":[TD([[makeQuery(id+"F0.imprint","IMPRINT",EDGE,{"disambiguationData":[TD([[subQ2,-1.0]])],"derivedFrom":subQ1}),-1.0]])]});}
            var Q66;
            {var subQ0=sQuery(id+"F0.wireOp",EDGE,"E19");var subQ1=sQuery(id+"F0.wireOp",EDGE,"E9");var subQ2=makeQuery(id+"F0.imprint","INTERSECT",VERTEX,{"derivedFrom":[subQ1,subQ0]});Q66=makeQuery(id+"F0.imprint","IMPRINT",FACE,{"disambiguationData":[TD([[makeQuery(id+"F0.imprint","IMPRINT",EDGE,{"disambiguationData":[TD([[subQ2,-1.0]])],"derivedFrom":subQ1}),1.0]])]});}
            var Q67;
            {var subQ0=sQuery(id+"F0.wireOp",EDGE,"E19");var subQ1=sQuery(id+"F0.wireOp",EDGE,"E11");var subQ2=makeQuery(id+"F0.imprint","INTERSECT",VERTEX,{"derivedFrom":[subQ1,subQ0]});Q67=makeQuery(id+"F0.imprint","IMPRINT",FACE,{"disambiguationData":[TD([[makeQuery(id+"F0.imprint","IMPRINT",EDGE,{"disambiguationData":[TD([[subQ2,-1.0]])],"derivedFrom":subQ1}),-1.0]])]});}
            var Q68;
            {var subQ0=sQuery(id+"F0.wireOp",EDGE,"E82");var subQ1=sQuery(id+"F0.wireOp",EDGE,"E12");var subQ2=makeQuery(id+"F0.imprint","INTERSECT",VERTEX,{"derivedFrom":[subQ1,subQ0]});Q68=makeQuery(id+"F0.imprint","IMPRINT",FACE,{"disambiguationData":[TD([[makeQuery(id+"F0.imprint","IMPRINT",EDGE,{"disambiguationData":[TD([[subQ2,1.0]])],"derivedFrom":subQ1}),-1.0]])]});}
            var Q69;
            {var subQ0=sQuery(id+"F0.wireOp",EDGE,"E82");var subQ1=sQuery(id+"F0.wireOp",EDGE,"E19");var subQ2=makeQuery(id+"F0.imprint","INTERSECT",VERTEX,{"derivedFrom":[subQ1,subQ0]});Q69=makeQuery(id+"F0.imprint","IMPRINT",FACE,{"disambiguationData":[TD([[makeQuery(id+"F0.imprint","IMPRINT",EDGE,{"disambiguationData":[TD([[subQ2,-1.0]])],"derivedFrom":subQ1}),-1.0]])]});}
            var Q70;
            {var subQ0=sQuery(id+"F0.wireOp",EDGE,"E84");var subQ1=sQuery(id+"F0.wireOp",EDGE,"E51");var subQ2=makeQuery(id+"F0.imprint","INTERSECT",VERTEX,{"derivedFrom":[subQ1,subQ0]});Q70=makeQuery(id+"F0.imprint","IMPRINT",FACE,{"disambiguationData":[TD([[makeQuery(id+"F0.imprint","IMPRINT",EDGE,{"disambiguationData":[TD([[subQ2,-1.0]])],"derivedFrom":subQ1}),-1.0]])]});}
            var Q71;
            {var subQ0=sQuery(id+"F0.wireOp",EDGE,"E83");var subQ1=sQuery(id+"F0.wireOp",EDGE,"E48");var subQ2=makeQuery(id+"F0.imprint","INTERSECT",VERTEX,{"derivedFrom":[subQ1,subQ0]});Q71=makeQuery(id+"F0.imprint","IMPRINT",FACE,{"disambiguationData":[TD([[makeQuery(id+"F0.imprint","IMPRINT",EDGE,{"disambiguationData":[TD([[subQ2,-1.0]])],"derivedFrom":subQ1}),1.0]])]});}
            var Q72;
            {var subQ0=sQuery(id+"F0.wireOp",EDGE,"E83");var subQ1=sQuery(id+"F0.wireOp",EDGE,"E50");var subQ2=makeQuery(id+"F0.imprint","INTERSECT",VERTEX,{"derivedFrom":[subQ1,subQ0]});Q72=makeQuery(id+"F0.imprint","IMPRINT",FACE,{"disambiguationData":[TD([[makeQuery(id+"F0.imprint","IMPRINT",EDGE,{"disambiguationData":[TD([[subQ2,1.0]])],"derivedFrom":subQ1}),1.0]])]});}
            var Q73;
            {var subQ0=sQuery(id+"F0.wireOp",EDGE,"E84");var subQ1=sQuery(id+"F0.wireOp",EDGE,"E49");var subQ2=makeQuery(id+"F0.imprint","INTERSECT",VERTEX,{"derivedFrom":[subQ1,subQ0]});Q73=makeQuery(id+"F0.imprint","IMPRINT",FACE,{"disambiguationData":[TD([[makeQuery(id+"F0.imprint","IMPRINT",EDGE,{"disambiguationData":[TD([[subQ2,-1.0]])],"derivedFrom":subQ1}),1.0]])]});}
            var Q74;
            {var subQ0=sQuery(id+"F0.wireOp",EDGE,"E84");var subQ1=sQuery(id+"F0.wireOp",EDGE,"E83");var subQ2=makeQuery(id+"F0.imprint","INTERSECT",VERTEX,{"derivedFrom":[subQ1,subQ0]});Q74=makeQuery(id+"F0.imprint","IMPRINT",FACE,{"disambiguationData":[TD([[makeQuery(id+"F0.imprint","IMPRINT",EDGE,{"disambiguationData":[TD([[subQ2,-1.0]])],"derivedFrom":subQ1}),-1.0]])]});}
            var Q75;
            {var subQ0=sQuery(id+"F0.wireOp",EDGE,"E21");var subQ1=sQuery(id+"F0.wireOp",EDGE,"E13");var subQ2=makeQuery(id+"F0.imprint","INTERSECT",VERTEX,{"derivedFrom":[subQ1,subQ0]});Q75=makeQuery(id+"F0.imprint","IMPRINT",FACE,{"disambiguationData":[TD([[makeQuery(id+"F0.imprint","IMPRINT",EDGE,{"disambiguationData":[TD([[subQ2,-1.0]])],"derivedFrom":subQ1}),1.0]])]});}
            var Q76;
            {var subQ0=sQuery(id+"F0.wireOp",EDGE,"E20");var subQ1=sQuery(id+"F0.wireOp",EDGE,"E14");var subQ2=makeQuery(id+"F0.imprint","INTERSECT",VERTEX,{"derivedFrom":[subQ1,subQ0]});Q76=makeQuery(id+"F0.imprint","IMPRINT",FACE,{"disambiguationData":[TD([[makeQuery(id+"F0.imprint","IMPRINT",EDGE,{"disambiguationData":[TD([[subQ2,-1.0]])],"derivedFrom":subQ1}),1.0]])]});}
            var Q77;
            {var subQ0=sQuery(id+"F0.wireOp",EDGE,"E89");var subQ1=sQuery(id+"F0.wireOp",EDGE,"E52");var subQ2=makeQuery(id+"F0.imprint","INTERSECT",VERTEX,{"derivedFrom":[subQ1,subQ0]});Q77=makeQuery(id+"F0.imprint","IMPRINT",FACE,{"disambiguationData":[TD([[makeQuery(id+"F0.imprint","IMPRINT",EDGE,{"disambiguationData":[TD([[subQ2,-1.0]])],"derivedFrom":subQ1}),-1.0]])]});}
            var Q78;
            {var subQ0=sQuery(id+"F0.wireOp",EDGE,"E90");var subQ1=sQuery(id+"F0.wireOp",EDGE,"E55");var subQ2=makeQuery(id+"F0.imprint","INTERSECT",VERTEX,{"derivedFrom":[subQ1,subQ0]});Q78=makeQuery(id+"F0.imprint","IMPRINT",FACE,{"disambiguationData":[TD([[makeQuery(id+"F0.imprint","IMPRINT",EDGE,{"disambiguationData":[TD([[subQ2,-1.0]])],"derivedFrom":subQ1}),1.0]])]});}
            var Q79;
            {var subQ0=sQuery(id+"F0.wireOp",EDGE,"E90");var subQ1=sQuery(id+"F0.wireOp",EDGE,"E89");var subQ2=makeQuery(id+"F0.imprint","INTERSECT",VERTEX,{"derivedFrom":[subQ1,subQ0]});Q79=makeQuery(id+"F0.imprint","IMPRINT",FACE,{"disambiguationData":[TD([[makeQuery(id+"F0.imprint","IMPRINT",EDGE,{"disambiguationData":[TD([[subQ2,-1.0]])],"derivedFrom":subQ1}),1.0]])]});}
            var Q80;
            {var subQ0=sQuery(id+"F0.wireOp",EDGE,"E90");var subQ1=sQuery(id+"F0.wireOp",EDGE,"E53");var subQ2=makeQuery(id+"F0.imprint","INTERSECT",VERTEX,{"derivedFrom":[subQ1,subQ0]});Q80=makeQuery(id+"F0.imprint","IMPRINT",FACE,{"disambiguationData":[TD([[makeQuery(id+"F0.imprint","IMPRINT",EDGE,{"disambiguationData":[TD([[subQ2,-1.0]])],"derivedFrom":subQ1}),-1.0]])]});}
            var Q81;
            {var subQ0=sQuery(id+"F0.wireOp",EDGE,"E89");var subQ1=sQuery(id+"F0.wireOp",EDGE,"E54");var subQ2=makeQuery(id+"F0.imprint","INTERSECT",VERTEX,{"derivedFrom":[subQ1,subQ0]});Q81=makeQuery(id+"F0.imprint","IMPRINT",FACE,{"disambiguationData":[TD([[makeQuery(id+"F0.imprint","IMPRINT",EDGE,{"disambiguationData":[TD([[subQ2,1.0]])],"derivedFrom":subQ1}),-1.0]])]});}
            var Q82;
            {var subQ0=sQuery(id+"F0.wireOp",EDGE,"E86");var subQ1=sQuery(id+"F0.wireOp",EDGE,"E59");var subQ2=makeQuery(id+"F0.imprint","INTERSECT",VERTEX,{"derivedFrom":[subQ1,subQ0]});Q82=makeQuery(id+"F0.imprint","IMPRINT",FACE,{"disambiguationData":[TD([[makeQuery(id+"F0.imprint","IMPRINT",EDGE,{"disambiguationData":[TD([[subQ2,1.0]])],"derivedFrom":subQ1}),1.0]])]});}
            var Q83;
            {var subQ0=sQuery(id+"F0.wireOp",EDGE,"E85");var subQ1=sQuery(id+"F0.wireOp",EDGE,"E56");var subQ2=makeQuery(id+"F0.imprint","INTERSECT",VERTEX,{"derivedFrom":[subQ1,subQ0]});Q83=makeQuery(id+"F0.imprint","IMPRINT",FACE,{"disambiguationData":[TD([[makeQuery(id+"F0.imprint","IMPRINT",EDGE,{"disambiguationData":[TD([[subQ2,-1.0]])],"derivedFrom":subQ1}),1.0]])]});}
            var Q84;
            {var subQ0=sQuery(id+"F0.wireOp",EDGE,"E85");var subQ1=sQuery(id+"F0.wireOp",EDGE,"E58");var subQ2=makeQuery(id+"F0.imprint","INTERSECT",VERTEX,{"derivedFrom":[subQ1,subQ0]});Q84=makeQuery(id+"F0.imprint","IMPRINT",FACE,{"disambiguationData":[TD([[makeQuery(id+"F0.imprint","IMPRINT",EDGE,{"disambiguationData":[TD([[subQ2,1.0]])],"derivedFrom":subQ1}),1.0]])]});}
            var Q85;
            {var subQ0=sQuery(id+"F0.wireOp",EDGE,"E86");var subQ1=sQuery(id+"F0.wireOp",EDGE,"E57");var subQ2=makeQuery(id+"F0.imprint","INTERSECT",VERTEX,{"derivedFrom":[subQ1,subQ0]});Q85=makeQuery(id+"F0.imprint","IMPRINT",FACE,{"disambiguationData":[TD([[makeQuery(id+"F0.imprint","IMPRINT",EDGE,{"disambiguationData":[TD([[subQ2,-1.0]])],"derivedFrom":subQ1}),1.0]])]});}
            var Q86;
            {var subQ0=sQuery(id+"F0.wireOp",EDGE,"E86");var subQ1=sQuery(id+"F0.wireOp",EDGE,"E85");var subQ2=makeQuery(id+"F0.imprint","INTERSECT",VERTEX,{"derivedFrom":[subQ1,subQ0]});Q86=makeQuery(id+"F0.imprint","IMPRINT",FACE,{"disambiguationData":[TD([[makeQuery(id+"F0.imprint","IMPRINT",EDGE,{"disambiguationData":[TD([[subQ2,-1.0]])],"derivedFrom":subQ1}),-1.0]])]});}
            var Q87;
            {var subQ0=sQuery(id+"F0.wireOp",EDGE,"E87");var subQ1=sQuery(id+"F0.wireOp",EDGE,"E77");var subQ2=makeQuery(id+"F0.imprint","INTERSECT",VERTEX,{"derivedFrom":[subQ1,subQ0]});Q87=makeQuery(id+"F0.imprint","IMPRINT",FACE,{"disambiguationData":[TD([[makeQuery(id+"F0.imprint","IMPRINT",EDGE,{"disambiguationData":[TD([[subQ2,1.0]])],"derivedFrom":subQ1}),1.0]])]});}
            var Q88;
            {var subQ0=sQuery(id+"F0.wireOp",EDGE,"E88");var subQ1=sQuery(id+"F0.wireOp",EDGE,"E74");var subQ2=makeQuery(id+"F0.imprint","INTERSECT",VERTEX,{"derivedFrom":[subQ1,subQ0]});Q88=makeQuery(id+"F0.imprint","IMPRINT",FACE,{"disambiguationData":[TD([[makeQuery(id+"F0.imprint","IMPRINT",EDGE,{"disambiguationData":[TD([[subQ2,-1.0]])],"derivedFrom":subQ1}),1.0]])]});}
            var Q89;
            {var subQ0=sQuery(id+"F0.wireOp",EDGE,"E88");var subQ1=sQuery(id+"F0.wireOp",EDGE,"E87");var subQ2=makeQuery(id+"F0.imprint","INTERSECT",VERTEX,{"derivedFrom":[subQ1,subQ0]});Q89=makeQuery(id+"F0.imprint","IMPRINT",FACE,{"disambiguationData":[TD([[makeQuery(id+"F0.imprint","IMPRINT",EDGE,{"disambiguationData":[TD([[subQ2,-1.0]])],"derivedFrom":subQ1}),1.0]])]});}
            var Q90;
            {var subQ0=sQuery(id+"F0.wireOp",EDGE,"E88");var subQ1=sQuery(id+"F0.wireOp",EDGE,"E76");var subQ2=makeQuery(id+"F0.imprint","INTERSECT",VERTEX,{"derivedFrom":[subQ1,subQ0]});Q90=makeQuery(id+"F0.imprint","IMPRINT",FACE,{"disambiguationData":[TD([[makeQuery(id+"F0.imprint","IMPRINT",EDGE,{"disambiguationData":[TD([[subQ2,1.0]])],"derivedFrom":subQ1}),1.0]])]});}
            var Q91;
            {var subQ0=sQuery(id+"F0.wireOp",EDGE,"E87");var subQ1=sQuery(id+"F0.wireOp",EDGE,"E75");var subQ2=makeQuery(id+"F0.imprint","INTERSECT",VERTEX,{"derivedFrom":[subQ1,subQ0]});Q91=makeQuery(id+"F0.imprint","IMPRINT",FACE,{"disambiguationData":[TD([[makeQuery(id+"F0.imprint","IMPRINT",EDGE,{"disambiguationData":[TD([[subQ2,-1.0]])],"derivedFrom":subQ1}),1.0]])]});}
            var Q92;
            {var subQ0=sQuery(id+"F0.wireOp",EDGE,"E91");var subQ1=sQuery(id+"F0.wireOp",EDGE,"E63");var subQ2=makeQuery(id+"F0.imprint","INTERSECT",VERTEX,{"derivedFrom":[subQ1,subQ0]});Q92=makeQuery(id+"F0.imprint","IMPRINT",FACE,{"disambiguationData":[TD([[makeQuery(id+"F0.imprint","IMPRINT",EDGE,{"disambiguationData":[TD([[subQ2,1.0]])],"derivedFrom":subQ1}),1.0]])]});}
            var Q93;
            {var subQ0=sQuery(id+"F0.wireOp",EDGE,"E92");var subQ1=sQuery(id+"F0.wireOp",EDGE,"E60");var subQ2=makeQuery(id+"F0.imprint","INTERSECT",VERTEX,{"derivedFrom":[subQ1,subQ0]});Q93=makeQuery(id+"F0.imprint","IMPRINT",FACE,{"disambiguationData":[TD([[makeQuery(id+"F0.imprint","IMPRINT",EDGE,{"disambiguationData":[TD([[subQ2,-1.0]])],"derivedFrom":subQ1}),1.0]])]});}
            var Q94;
            {var subQ0=sQuery(id+"F0.wireOp",EDGE,"E91");var subQ1=sQuery(id+"F0.wireOp",EDGE,"E61");var subQ2=makeQuery(id+"F0.imprint","INTERSECT",VERTEX,{"derivedFrom":[subQ1,subQ0]});Q94=makeQuery(id+"F0.imprint","IMPRINT",FACE,{"disambiguationData":[TD([[makeQuery(id+"F0.imprint","IMPRINT",EDGE,{"disambiguationData":[TD([[subQ2,-1.0]])],"derivedFrom":subQ1}),1.0]])]});}
            var Q95;
            {var subQ0=sQuery(id+"F0.wireOp",EDGE,"E92");var subQ1=sQuery(id+"F0.wireOp",EDGE,"E62");var subQ2=makeQuery(id+"F0.imprint","INTERSECT",VERTEX,{"derivedFrom":[subQ1,subQ0]});Q95=makeQuery(id+"F0.imprint","IMPRINT",FACE,{"disambiguationData":[TD([[makeQuery(id+"F0.imprint","IMPRINT",EDGE,{"disambiguationData":[TD([[subQ2,1.0]])],"derivedFrom":subQ1}),1.0]])]});}
            var Q96;
            {var subQ0=sQuery(id+"F0.wireOp",EDGE,"E92");var subQ1=sQuery(id+"F0.wireOp",EDGE,"E91");var subQ2=makeQuery(id+"F0.imprint","INTERSECT",VERTEX,{"derivedFrom":[subQ1,subQ0]});Q96=makeQuery(id+"F0.imprint","IMPRINT",FACE,{"disambiguationData":[TD([[makeQuery(id+"F0.imprint","IMPRINT",EDGE,{"disambiguationData":[TD([[subQ2,-1.0]])],"derivedFrom":subQ1}),1.0]])]});}
            var Q97;
            {var subQ0=sQuery(id+"F0.wireOp",EDGE,"E93");var subQ1=sQuery(id+"F0.wireOp",EDGE,"E81");var subQ2=makeQuery(id+"F0.imprint","INTERSECT",VERTEX,{"derivedFrom":[subQ1,subQ0]});Q97=makeQuery(id+"F0.imprint","IMPRINT",FACE,{"disambiguationData":[TD([[makeQuery(id+"F0.imprint","IMPRINT",EDGE,{"disambiguationData":[TD([[subQ2,1.0]])],"derivedFrom":subQ1}),1.0]])]});}
            var Q98;
            {var subQ0=sQuery(id+"F0.wireOp",EDGE,"E94");var subQ1=sQuery(id+"F0.wireOp",EDGE,"E78");var subQ2=makeQuery(id+"F0.imprint","INTERSECT",VERTEX,{"derivedFrom":[subQ1,subQ0]});Q98=makeQuery(id+"F0.imprint","IMPRINT",FACE,{"disambiguationData":[TD([[makeQuery(id+"F0.imprint","IMPRINT",EDGE,{"disambiguationData":[TD([[subQ2,-1.0]])],"derivedFrom":subQ1}),1.0]])]});}
            var Q99;
            {var subQ0=sQuery(id+"F0.wireOp",EDGE,"E94");var subQ1=sQuery(id+"F0.wireOp",EDGE,"E93");var subQ2=makeQuery(id+"F0.imprint","INTERSECT",VERTEX,{"derivedFrom":[subQ1,subQ0]});Q99=makeQuery(id+"F0.imprint","IMPRINT",FACE,{"disambiguationData":[TD([[makeQuery(id+"F0.imprint","IMPRINT",EDGE,{"disambiguationData":[TD([[subQ2,-1.0]])],"derivedFrom":subQ1}),1.0]])]});}
            var Q100;
            {var subQ0=sQuery(id+"F0.wireOp",EDGE,"E94");var subQ1=sQuery(id+"F0.wireOp",EDGE,"E80");var subQ2=makeQuery(id+"F0.imprint","INTERSECT",VERTEX,{"derivedFrom":[subQ1,subQ0]});Q100=makeQuery(id+"F0.imprint","IMPRINT",FACE,{"disambiguationData":[TD([[makeQuery(id+"F0.imprint","IMPRINT",EDGE,{"disambiguationData":[TD([[subQ2,1.0]])],"derivedFrom":subQ1}),1.0]])]});}
            var Q101;
            {var subQ0=sQuery(id+"F0.wireOp",EDGE,"E93");var subQ1=sQuery(id+"F0.wireOp",EDGE,"E79");var subQ2=makeQuery(id+"F0.imprint","INTERSECT",VERTEX,{"derivedFrom":[subQ1,subQ0]});Q101=makeQuery(id+"F0.imprint","IMPRINT",FACE,{"disambiguationData":[TD([[makeQuery(id+"F0.imprint","IMPRINT",EDGE,{"disambiguationData":[TD([[subQ2,-1.0]])],"derivedFrom":subQ1}),1.0]])]});}
            var Q102;
            {var subQ0=sQuery(id+"F0.wireOp",EDGE,"E20");var subQ1=sQuery(id+"F0.wireOp",EDGE,"E16");var subQ2=makeQuery(id+"F0.imprint","INTERSECT",VERTEX,{"derivedFrom":[subQ1,subQ0]});Q102=makeQuery(id+"F0.imprint","IMPRINT",FACE,{"disambiguationData":[TD([[makeQuery(id+"F0.imprint","IMPRINT",EDGE,{"disambiguationData":[TD([[subQ2,1.0]])],"derivedFrom":subQ1}),1.0]])]});}
            var Q103;
            {var subQ0=sQuery(id+"F0.wireOp",EDGE,"E21");var subQ1=sQuery(id+"F0.wireOp",EDGE,"E15");var subQ2=makeQuery(id+"F0.imprint","INTERSECT",VERTEX,{"derivedFrom":[subQ1,subQ0]});Q103=makeQuery(id+"F0.imprint","IMPRINT",FACE,{"disambiguationData":[TD([[makeQuery(id+"F0.imprint","IMPRINT",EDGE,{"disambiguationData":[TD([[subQ2,1.0]])],"derivedFrom":subQ1}),1.0]])]});}
            var Q104;
            {var subQ0=sQuery(id+"F0.wireOp",EDGE,"E21");var subQ1=sQuery(id+"F0.wireOp",EDGE,"E20");var subQ2=makeQuery(id+"F0.imprint","INTERSECT",VERTEX,{"derivedFrom":[subQ1,subQ0]});Q104=makeQuery(id+"F0.imprint","IMPRINT",FACE,{"disambiguationData":[TD([[makeQuery(id+"F0.imprint","IMPRINT",EDGE,{"disambiguationData":[TD([[subQ2,-1.0]])],"derivedFrom":subQ1}),1.0]])]});}
            extrude(context, id + "F11", {"entities" : qUnion([Q0, Q1, Q2, Q3, Q4, Q5, Q6, Q7, Q8, Q9, Q10, Q11, Q12, Q13, Q14, Q15, Q16, Q17, Q18, Q19, Q20, Q21, Q22, Q23, Q24, Q25, Q26, Q27, Q28, Q29, Q30, Q31, Q32, Q33, Q34, Q35, Q36, Q37, Q38, Q39, Q40, Q41, Q42, Q43, Q44, Q45, Q46, Q47, Q48, Q49, Q50, Q51, Q52, Q53, Q54, Q55, Q56, Q57, Q58, Q59, Q60, Q61, Q62, Q63, Q64, Q65, Q66, Q67, Q68, Q69, Q70, Q71, Q72, Q73, Q74, Q75, Q76, Q77, Q78, Q79, Q80, Q81, Q82, Q83, Q84, Q85, Q86, Q87, Q88, Q89, Q90, Q91, Q92, Q93, Q94, Q95, Q96, Q97, Q98, Q99, Q100, Q101, Q102, Q103, Q104]), "operationType" : NewBodyOperationType.ADD, "depth" : 35.23 * mm, "offsetDistance" : 25.4 * mm});
        }
        {
            var Q0;
            Q0=makeQuery(id+"F0.imprint","IMPRINT",FACE,{"disambiguationData":[TD([[makeQuery(id+"F0.imprint","IMPRINT",EDGE,{"derivedFrom":sQuery(id+"F0.wireOp",EDGE,"E102.bottom")}),1.0]])]});
            extrude(context, id + "F12", {"entities" : qUnion([Q0]), "operationType" : NewBodyOperationType.ADD, "depth" : 36.35 * mm, "offsetDistance" : 25.4 * mm});
        }
    });
